# Revit family: 879-003X99-001-DN300-600
name_source: partatom
category: Pipe Accessories
units: mm (PartAtom-declared; Revit-internal decimal feet)

## family parameters
Always vertical = Yes
Cut with Voids When Loaded = No
Part Type = Valve - Breaks Into
Round Connector Dimension = Use Diameter
Shared = No
Work Plane-Based = No

## types (59) — shared parameters
879-0300-00-04400309999 = DN300_PN10
879-0300-00-04400319999 = DN300_PN10
879-0300-00-044003199A0 = DN300_PN10
879-0300-00-04400329999 = DN300_PN10
879-0300-00-04400339999 = DN300_PN10
879-0300-00-14400309999 = DN300_PN16
879-0300-00-14400319999 = DN300_PN16
879-0300-00-144003199A0 = DN300_PN16
879-0300-00-14400329999 = DN300_PN16
879-0300-00-14400339999 = DN300_PN16
879-0350-00-04400309999 = DN350_PN10
879-0350-00-04400319999 = DN350_PN10
879-0350-00-044003199A0 = DN350_PN10
879-0350-00-04400329999 = DN350_PN10
879-0350-00-04400339999 = DN350_PN10
879-0350-00-14400309999 = DN350_PN16
879-0350-00-14400319999 = DN350_PN16
879-0350-00-144003199A0 = DN350_PN16
879-0350-00-14400329999 = DN350_PN16
879-0350-00-14400339999 = DN350_PN16
879-0400-00-04400309999 = DN400_PN10
879-0400-00-04400319999 = DN400_PN10
879-0400-00-044003199A0 = DN400_PN10
879-0400-00-04400329999 = DN400_PN10
879-0400-00-04400339999 = DN400_PN10
879-0400-00-14400309999 = DN400_PN16
879-0400-00-14400319999 = DN400_PN16
879-0400-00-144003199A0 = DN400_PN16
879-0400-00-14400329999 = DN400_PN16
879-0400-00-14400339999 = DN400_PN16
879-0450-00-04400309999 = DN450_PN10
879-0450-00-04400319999 = DN450_PN10
879-0450-00-044003199A0 = DN450_PN10
879-0450-00-04400329999 = DN450_PN10
879-0450-00-04400339999 = DN450_PN10
879-0450-00-14400309999 = DN450_PN16
879-0450-00-14400319999 = DN450_PN16
879-0450-00-144003199A0 = DN450_PN16
879-0450-00-14400329999 = DN450_PN16
879-0450-00-14400339999 = DN450_PN16
879-0500-00-04400309999 = DN500_PN10
879-0500-00-04400319999 = DN500_PN10
879-0500-00-044003199A0 = DN500_PN10
879-0500-00-04400329999 = DN500_PN10
879-0500-00-04400339999 = DN500_PN10
879-0500-00-14400309999 = DN500_PN16
879-0500-00-14400319999 = DN500_PN16
879-0500-00-144003199A0 = DN500_PN16
879-0500-00-14400329999 = DN500_PN16
879-0500-00-14400339999 = DN500_PN16
879-0600-00-04400309999 = DN600_PN10
879-0600-00-04400319999 = DN600_PN10
879-0600-00-044003199A0 = DN600_PN10
879-0600-00-04400329999 = DN600_PN10
879-0600-00-04400339999 = DN600_PN10
879-0600-00-14400309999 = DN600_PN16
879-0600-00-14400319999 = DN600_PN16
879-0600-00-144003199A0 = DN600_PN16
879-0600-00-14400329999 = DN600_PN16
879-0600-00-14400339999 = DN600_PN16
Body_wall_thickness = 10 mm  [stored 0.0328084 ft]
Description_ = AVK ONE WAY ALTITUDE LEVEL CONTROL VALVE
Search_Table = 879-003X99-001-DN300-600
URL product pages = https://www.avkvalves.com

## per-type parameters (varying)
- 879-0300-00-04400309999_DN300_PN10: Body_Collar_Dia=77 mm; Body_Collar_Dia_2=53 mm; Body_Flange_Dia=243 mm; Body_Flange_Dia_2=266 mm; Body_Height_1=213 mm; Body_Height_2=106 mm; Body_Height_3=95 mm; Body_Height_4=121 mm; Body_Top_Dia=31 mm  [stored 0.101706 ft]; Body_Top_Dia_2=26 mm; Body_With_Dia=106 mm; Body_With_Dia_1=213 mm; Body_With_Dia_2=213 mm; Bolt_support=654 mm; Bolt_support_2=327 mm; Bolt_support_Dia=20 mm  [stored 0.0656168 ft]; Bolt_support_lenght=170 mm; Bolt_support_lenght_2=180 mm; Bottom_profile=75 mm; D1=185 mm; D3=223 mm; DN=300 mm; Fillet_Length=10 mm  [stored 0.0328084 ft]; Fillet_Length_Ref=30 mm  [stored 0.0984252 ft]; Flange_thickness=25 mm  [stored 0.082021 ft]; H=865 mm; H3_Ref=855 mm; ID=150 mm; L=850 mm; L_Ref=401 mm; NV_Dia=190 mm; PG_Dia=100 mm; PG_Ref=142 mm; PG_depth=14 mm  [stored 0.0459318 ft]; PG_height=519 mm; PG_height_1=469 mm; PG_ref=160 mm; PR_1=63 mm; P_lenght=116 mm; Pilot_Dia_1=53 mm; Pilot_Dia_2=105 mm; Pilot_Dia_3=35 mm  [stored 0.114829 ft]; Pilot_Dia_4=18 mm; Pilot_Dia_5=12 mm  [stored 0.0393701 ft]; Pilot_top_1=530 mm; Pilot_top_ref=92 mm; Profile1_Height=326 mm; Profile1_Length=60 mm; Profile1_Length_2=40 mm  [stored 0.131234 ft]; Profile_Dia=10 mm  [stored 0.0328084 ft]; Profile_Dia_2=10 mm  [stored 0.0328084 ft]; Profile_Dia_3=20 mm  [stored 0.0656168 ft]; Profile_Dia_Ref=5 mm  [stored 0.0164042 ft]; Profile_Dia_Ref_2=20 mm  [stored 0.0656168 ft]; Profile_height ref=30 mm  [stored 0.0984252 ft]; T_Height=277 mm; T_Height_2=237 mm; T_Height_Ref_1=40 mm  [stored 0.131234 ft]; T_Height_Ref_2=46 mm  [stored 0.150919 ft]; T_ref=481 mm; Top_Profile=392 mm; Top_Profile_Ref=397 mm; W=835 mm; W_Ref=821 mm
- 879-0300-00-04400319999_DN300_PN10: Body_Collar_Dia=77 mm; Body_Collar_Dia_2=53 mm; Body_Flange_Dia=243 mm; Body_Flange_Dia_2=266 mm; Body_Height_1=213 mm; Body_Height_2=106 mm; Body_Height_3=106 mm; Body_Height_4=121 mm; Body_Top_Dia=31 mm  [stored 0.101706 ft]; Body_Top_Dia_2=26 mm; Body_With_Dia=106 mm; Body_With_Dia_1=213 mm; Body_With_Dia_2=213 mm; Bolt_support=654 mm; Bolt_support_2=327 mm; Bolt_support_Dia=20 mm  [stored 0.0656168 ft]; Bolt_support_lenght=170 mm; Bolt_support_lenght_2=180 mm; Bottom_profile=75 mm; D1=185 mm; D3=223 mm; DN=300 mm; Fillet_Length=10 mm  [stored 0.0328084 ft]; Fillet_Length_Ref=30 mm  [stored 0.0984252 ft]; Flange_thickness=25 mm  [stored 0.082021 ft]; H=865 mm; H3_Ref=855 mm; ID=150 mm; L=850 mm; L_Ref=401 mm; NV_Dia=190 mm; PG_Dia=100 mm; PG_Ref=142 mm; PG_depth=14 mm  [stored 0.0459318 ft]; PG_height=549 mm; PG_height_1=499 mm; PG_ref=160 mm; PR_1=54 mm; P_lenght=116 mm; Pilot_Dia_1=53 mm; Pilot_Dia_2=105 mm; Pilot_Dia_3=35 mm  [stored 0.114829 ft]; Pilot_Dia_4=18 mm; Pilot_Dia_5=12 mm  [stored 0.0393701 ft]; Pilot_top_1=536 mm; Pilot_top_ref=86 mm; Profile1_Height=365 mm; Profile1_Length=60 mm; Profile1_Length_2=40 mm  [stored 0.131234 ft]; Profile_Dia=10 mm  [stored 0.0328084 ft]; Profile_Dia_2=10 mm  [stored 0.0328084 ft]; Profile_Dia_3=20 mm  [stored 0.0656168 ft]; Profile_Dia_Ref=5 mm  [stored 0.0164042 ft]; Profile_Dia_Ref_2=20 mm  [stored 0.0656168 ft]; Profile_height ref=30 mm  [stored 0.0984252 ft]; T_Height=238 mm; T_Height_2=204 mm; T_Height_Ref_1=34 mm; T_Height_Ref_2=40 mm  [stored 0.131234 ft]; T_ref=502 mm; Top_Profile=392 mm; Top_Profile_Ref=397 mm; W=835 mm; W_Ref=821 mm
- 879-0300-00-044003199A0_DN300_PN10: Body_Collar_Dia=77 mm; Body_Collar_Dia_2=53 mm; Body_Flange_Dia=243 mm; Body_Flange_Dia_2=266 mm; Body_Height_1=213 mm; Body_Height_2=106 mm; Body_Height_3=95 mm; Body_Height_4=121 mm; Body_Top_Dia=31 mm  [stored 0.101706 ft]; Body_Top_Dia_2=26 mm; Body_With_Dia=106 mm; Body_With_Dia_1=213 mm; Body_With_Dia_2=213 mm; Bolt_support=654 mm; Bolt_support_2=327 mm; Bolt_support_Dia=20 mm  [stored 0.0656168 ft]; Bolt_support_lenght=170 mm; Bolt_support_lenght_2=180 mm; Bottom_profile=75 mm; D1=185 mm; D3=223 mm; DN=300 mm; Fillet_Length=10 mm  [stored 0.0328084 ft]; Fillet_Length_Ref=30 mm  [stored 0.0984252 ft]; Flange_thickness=25 mm  [stored 0.082021 ft]; H=881 mm; H3_Ref=871 mm; ID=150 mm; L=850 mm; L_Ref=401 mm; NV_Dia=190 mm; PG_Dia=100 mm; PG_Ref=142 mm; PG_depth=14 mm  [stored 0.0459318 ft]; PG_height=537 mm; PG_height_1=487 mm; PG_ref=160 mm; PR_1=62 mm; P_lenght=120 mm; Pilot_Dia_1=55 mm; Pilot_Dia_2=109 mm; Pilot_Dia_3=36 mm  [stored 0.11811 ft]; Pilot_Dia_4=18 mm; Pilot_Dia_5=12 mm  [stored 0.0393701 ft]; Pilot_top_1=538 mm; Pilot_top_ref=100 mm; Profile1_Height=345 mm; Profile1_Length=60 mm; Profile1_Length_2=40 mm  [stored 0.131234 ft]; Profile_Dia=10 mm  [stored 0.0328084 ft]; Profile_Dia_2=10 mm  [stored 0.0328084 ft]; Profile_Dia_3=20 mm  [stored 0.0656168 ft]; Profile_Dia_Ref=5 mm  [stored 0.0164042 ft]; Profile_Dia_Ref_2=20 mm  [stored 0.0656168 ft]; Profile_height ref=30 mm  [stored 0.0984252 ft]; T_Height=274 mm; T_Height_2=234 mm; T_Height_Ref_1=39 mm  [stored 0.127953 ft]; T_Height_Ref_2=46 mm  [stored 0.150919 ft]; T_ref=499 mm; Top_Profile=392 mm; Top_Profile_Ref=397 mm; W=835 mm; W_Ref=821 mm
- 879-0300-00-04400329999_DN300_PN10: Body_Collar_Dia=77 mm; Body_Collar_Dia_2=53 mm; Body_Flange_Dia=243 mm; Body_Flange_Dia_2=266 mm; Body_Height_1=213 mm; Body_Height_2=106 mm; Body_Height_3=95 mm; Body_Height_4=121 mm; Body_Top_Dia=31 mm  [stored 0.101706 ft]; Body_Top_Dia_2=26 mm; Body_With_Dia=106 mm; Body_With_Dia_1=213 mm; Body_With_Dia_2=213 mm; Bolt_support=654 mm; Bolt_support_2=327 mm; Bolt_support_Dia=20 mm  [stored 0.0656168 ft]; Bolt_support_lenght=170 mm; Bolt_support_lenght_2=180 mm; Bottom_profile=75 mm; D1=185 mm; D3=223 mm; DN=300 mm; Fillet_Length=10 mm  [stored 0.0328084 ft]; Fillet_Length_Ref=30 mm  [stored 0.0984252 ft]; Flange_thickness=25 mm  [stored 0.082021 ft]; H=865 mm; H3_Ref=855 mm; ID=150 mm; L=850 mm; L_Ref=401 mm; NV_Dia=190 mm; PG_Dia=100 mm; PG_Ref=142 mm; PG_depth=14 mm  [stored 0.0459318 ft]; PG_height=533 mm; PG_height_1=483 mm; PG_ref=160 mm; PR_1=58 mm; P_lenght=120 mm; Pilot_Dia_1=55 mm; Pilot_Dia_2=109 mm; Pilot_Dia_3=36 mm  [stored 0.11811 ft]; Pilot_Dia_4=18 mm; Pilot_Dia_5=12 mm  [stored 0.0393701 ft]; Pilot_top_1=530 mm; Pilot_top_ref=92 mm; Profile1_Height=345 mm; Profile1_Length=60 mm; Profile1_Length_2=40 mm  [stored 0.131234 ft]; Profile_Dia=10 mm  [stored 0.0328084 ft]; Profile_Dia_2=10 mm  [stored 0.0328084 ft]; Profile_Dia_3=20 mm  [stored 0.0656168 ft]; Profile_Dia_Ref=5 mm  [stored 0.0164042 ft]; Profile_Dia_Ref_2=20 mm  [stored 0.0656168 ft]; Profile_height ref=30 mm  [stored 0.0984252 ft]; T_Height=258 mm; T_Height_2=221 mm; T_Height_Ref_1=37 mm; T_Height_Ref_2=43 mm; T_ref=491 mm; Top_Profile=392 mm; Top_Profile_Ref=397 mm; W=835 mm; W_Ref=821 mm
- 879-0300-00-04400339999_DN300_PN10: Body_Collar_Dia=77 mm; Body_Collar_Dia_2=53 mm; Body_Flange_Dia=243 mm; Body_Flange_Dia_2=266 mm; Body_Height_1=213 mm; Body_Height_2=106 mm; Body_Height_3=95 mm; Body_Height_4=121 mm; Body_Top_Dia=31 mm  [stored 0.101706 ft]; Body_Top_Dia_2=26 mm; Body_With_Dia=106 mm; Body_With_Dia_1=213 mm; Body_With_Dia_2=213 mm; Bolt_support=654 mm; Bolt_support_2=327 mm; Bolt_support_Dia=20 mm  [stored 0.0656168 ft]; Bolt_support_lenght=170 mm; Bolt_support_lenght_2=180 mm; Bottom_profile=75 mm; D1=185 mm; D3=223 mm; DN=300 mm; Fillet_Length=10 mm  [stored 0.0328084 ft]; Fillet_Length_Ref=30 mm  [stored 0.0984252 ft]; Flange_thickness=25 mm  [stored 0.082021 ft]; H=865 mm; H3_Ref=855 mm; ID=150 mm; L=850 mm; L_Ref=401 mm; NV_Dia=190 mm; PG_Dia=100 mm; PG_Ref=142 mm; PG_depth=14 mm  [stored 0.0459318 ft]; PG_height=519 mm; PG_height_1=469 mm; PG_ref=160 mm; PR_1=63 mm; P_lenght=116 mm; Pilot_Dia_1=53 mm; Pilot_Dia_2=105 mm; Pilot_Dia_3=35 mm  [stored 0.114829 ft]; Pilot_Dia_4=18 mm; Pilot_Dia_5=12 mm  [stored 0.0393701 ft]; Pilot_top_1=530 mm; Pilot_top_ref=92 mm; Profile1_Height=326 mm; Profile1_Length=60 mm; Profile1_Length_2=40 mm  [stored 0.131234 ft]; Profile_Dia=10 mm  [stored 0.0328084 ft]; Profile_Dia_2=10 mm  [stored 0.0328084 ft]; Profile_Dia_3=20 mm  [stored 0.0656168 ft]; Profile_Dia_Ref=5 mm  [stored 0.0164042 ft]; Profile_Dia_Ref_2=20 mm  [stored 0.0656168 ft]; Profile_height ref=30 mm  [stored 0.0984252 ft]; T_Height=277 mm; T_Height_2=237 mm; T_Height_Ref_1=40 mm  [stored 0.131234 ft]; T_Height_Ref_2=46 mm  [stored 0.150919 ft]; T_ref=481 mm; Top_Profile=392 mm; Top_Profile_Ref=397 mm; W=835 mm; W_Ref=821 mm
- 879-0300-00-14400309999_DN300_PN16: Body_Collar_Dia=77 mm; Body_Collar_Dia_2=53 mm; Body_Flange_Dia=243 mm; Body_Flange_Dia_2=266 mm; Body_Height_1=213 mm; Body_Height_2=106 mm; Body_Height_3=106 mm; Body_Height_4=121 mm; Body_Top_Dia=31 mm  [stored 0.101706 ft]; Body_Top_Dia_2=26 mm; Body_With_Dia=106 mm; Body_With_Dia_1=213 mm; Body_With_Dia_2=213 mm; Bolt_support=654 mm; Bolt_support_2=327 mm; Bolt_support_Dia=20 mm  [stored 0.0656168 ft]; Bolt_support_lenght=170 mm; Bolt_support_lenght_2=180 mm; Bottom_profile=75 mm; D1=185 mm; D3=230 mm; DN=301 mm; Fillet_Length=10 mm  [stored 0.0328084 ft]; Fillet_Length_Ref=30 mm  [stored 0.0984252 ft]; Flange_thickness=25 mm  [stored 0.082021 ft]; H=865 mm; H3_Ref=855 mm; ID=150 mm; L=850 mm; L_Ref=401 mm; NV_Dia=190 mm; PG_Dia=100 mm; PG_Ref=142 mm; PG_depth=14 mm  [stored 0.0459318 ft]; PG_height=547 mm; PG_height_1=497 mm; PG_ref=160 mm; PR_1=52 mm; P_lenght=116 mm; Pilot_Dia_1=53 mm; Pilot_Dia_2=105 mm; Pilot_Dia_3=35 mm  [stored 0.114829 ft]; Pilot_Dia_4=18 mm; Pilot_Dia_5=12 mm  [stored 0.0393701 ft]; Pilot_top_1=532 mm; Pilot_top_ref=83 mm; Profile1_Height=365 mm; Profile1_Length=62 mm; Profile1_Length_2=41 mm; Profile_Dia=10 mm  [stored 0.0328084 ft]; Profile_Dia_2=10 mm  [stored 0.0328084 ft]; Profile_Dia_3=20 mm  [stored 0.0656168 ft]; Profile_Dia_Ref=5 mm  [stored 0.0164042 ft]; Profile_Dia_Ref_2=20 mm  [stored 0.0656168 ft]; Profile_height ref=30 mm  [stored 0.0984252 ft]; T_Height=230 mm; T_Height_2=197 mm; T_Height_Ref_1=33 mm; T_Height_Ref_2=38 mm  [stored 0.124672 ft]; T_ref=499 mm; Top_Profile=392 mm; Top_Profile_Ref=397 mm; W=835 mm; W_Ref=821 mm
- 879-0300-00-14400319999_DN300_PN16: Body_Collar_Dia=77 mm; Body_Collar_Dia_2=53 mm; Body_Flange_Dia=243 mm; Body_Flange_Dia_2=266 mm; Body_Height_1=213 mm; Body_Height_2=106 mm; Body_Height_3=95 mm; Body_Height_4=121 mm; Body_Top_Dia=31 mm  [stored 0.101706 ft]; Body_Top_Dia_2=26 mm; Body_With_Dia=106 mm; Body_With_Dia_1=213 mm; Body_With_Dia_2=213 mm; Bolt_support=654 mm; Bolt_support_2=327 mm; Bolt_support_Dia=20 mm  [stored 0.0656168 ft]; Bolt_support_lenght=170 mm; Bolt_support_lenght_2=180 mm; Bottom_profile=75 mm; D1=185 mm; D3=230 mm; DN=301 mm; Fillet_Length=10 mm  [stored 0.0328084 ft]; Fillet_Length_Ref=30 mm  [stored 0.0984252 ft]; Flange_thickness=25 mm  [stored 0.082021 ft]; H=865 mm; H3_Ref=855 mm; ID=150 mm; L=850 mm; L_Ref=401 mm; NV_Dia=190 mm; PG_Dia=100 mm; PG_Ref=142 mm; PG_depth=14 mm  [stored 0.0459318 ft]; PG_height=532 mm; PG_height_1=482 mm; PG_ref=160 mm; PR_1=57 mm; P_lenght=120 mm; Pilot_Dia_1=55 mm; Pilot_Dia_2=109 mm; Pilot_Dia_3=36 mm  [stored 0.11811 ft]; Pilot_Dia_4=18 mm; Pilot_Dia_5=12 mm  [stored 0.0393701 ft]; Pilot_top_1=527 mm; Pilot_top_ref=88 mm; Profile1_Height=345 mm; Profile1_Length=62 mm; Profile1_Length_2=41 mm; Profile_Dia=10 mm  [stored 0.0328084 ft]; Profile_Dia_2=10 mm  [stored 0.0328084 ft]; Profile_Dia_3=20 mm  [stored 0.0656168 ft]; Profile_Dia_Ref=5 mm  [stored 0.0164042 ft]; Profile_Dia_Ref_2=20 mm  [stored 0.0656168 ft]; Profile_height ref=30 mm  [stored 0.0984252 ft]; T_Height=250 mm; T_Height_2=214 mm; T_Height_Ref_1=36 mm  [stored 0.11811 ft]; T_Height_Ref_2=42 mm  [stored 0.137795 ft]; T_ref=488 mm; Top_Profile=392 mm; Top_Profile_Ref=397 mm; W=835 mm; W_Ref=821 mm
- 879-0300-00-144003199A0_DN300_PN16: Body_Collar_Dia=77 mm; Body_Collar_Dia_2=53 mm; Body_Flange_Dia=243 mm; Body_Flange_Dia_2=266 mm; Body_Height_1=213 mm; Body_Height_2=106 mm; Body_Height_3=95 mm; Body_Height_4=121 mm; Body_Top_Dia=31 mm  [stored 0.101706 ft]; Body_Top_Dia_2=26 mm; Body_With_Dia=106 mm; Body_With_Dia_1=213 mm; Body_With_Dia_2=213 mm; Bolt_support=654 mm; Bolt_support_2=327 mm; Bolt_support_Dia=20 mm  [stored 0.0656168 ft]; Bolt_support_lenght=170 mm; Bolt_support_lenght_2=180 mm; Bottom_profile=75 mm; D1=185 mm; D3=230 mm; DN=301 mm; Fillet_Length=10 mm  [stored 0.0328084 ft]; Fillet_Length_Ref=30 mm  [stored 0.0984252 ft]; Flange_thickness=25 mm  [stored 0.082021 ft]; H=881 mm; H3_Ref=871 mm; ID=150 mm; L=850 mm; L_Ref=401 mm; NV_Dia=190 mm; PG_Dia=100 mm; PG_Ref=142 mm; PG_depth=14 mm  [stored 0.0459318 ft]; PG_height=535 mm; PG_height_1=485 mm; PG_ref=160 mm; PR_1=60 mm; P_lenght=120 mm; Pilot_Dia_1=55 mm; Pilot_Dia_2=109 mm; Pilot_Dia_3=36 mm  [stored 0.11811 ft]; Pilot_Dia_4=18 mm; Pilot_Dia_5=12 mm  [stored 0.0393701 ft]; Pilot_top_1=535 mm; Pilot_top_ref=96 mm; Profile1_Height=345 mm; Profile1_Length=62 mm; Profile1_Length_2=41 mm; Profile_Dia=10 mm  [stored 0.0328084 ft]; Profile_Dia_2=10 mm  [stored 0.0328084 ft]; Profile_Dia_3=20 mm  [stored 0.0656168 ft]; Profile_Dia_Ref=5 mm  [stored 0.0164042 ft]; Profile_Dia_Ref_2=20 mm  [stored 0.0656168 ft]; Profile_height ref=30 mm  [stored 0.0984252 ft]; T_Height=266 mm; T_Height_2=228 mm; T_Height_Ref_1=38 mm  [stored 0.124672 ft]; T_Height_Ref_2=44 mm; T_ref=495 mm; Top_Profile=392 mm; Top_Profile_Ref=397 mm; W=835 mm; W_Ref=821 mm
- 879-0300-00-14400329999_DN300_PN16: Body_Collar_Dia=77 mm; Body_Collar_Dia_2=53 mm; Body_Flange_Dia=243 mm; Body_Flange_Dia_2=266 mm; Body_Height_1=213 mm; Body_Height_2=106 mm; Body_Height_3=95 mm; Body_Height_4=121 mm; Body_Top_Dia=31 mm  [stored 0.101706 ft]; Body_Top_Dia_2=26 mm; Body_With_Dia=106 mm; Body_With_Dia_1=213 mm; Body_With_Dia_2=213 mm; Bolt_support=654 mm; Bolt_support_2=327 mm; Bolt_support_Dia=20 mm  [stored 0.0656168 ft]; Bolt_support_lenght=170 mm; Bolt_support_lenght_2=180 mm; Bottom_profile=75 mm; D1=185 mm; D3=230 mm; DN=301 mm; Fillet_Length=10 mm  [stored 0.0328084 ft]; Fillet_Length_Ref=30 mm  [stored 0.0984252 ft]; Flange_thickness=25 mm  [stored 0.082021 ft]; H=865 mm; H3_Ref=855 mm; ID=150 mm; L=850 mm; L_Ref=401 mm; NV_Dia=190 mm; PG_Dia=100 mm; PG_Ref=142 mm; PG_depth=14 mm  [stored 0.0459318 ft]; PG_height=517 mm; PG_height_1=467 mm; PG_ref=160 mm; PR_1=61 mm; P_lenght=116 mm; Pilot_Dia_1=53 mm; Pilot_Dia_2=105 mm; Pilot_Dia_3=35 mm  [stored 0.114829 ft]; Pilot_Dia_4=18 mm; Pilot_Dia_5=12 mm  [stored 0.0393701 ft]; Pilot_top_1=527 mm; Pilot_top_ref=88 mm; Profile1_Height=326 mm; Profile1_Length=62 mm; Profile1_Length_2=41 mm; Profile_Dia=10 mm  [stored 0.0328084 ft]; Profile_Dia_2=10 mm  [stored 0.0328084 ft]; Profile_Dia_3=20 mm  [stored 0.0656168 ft]; Profile_Dia_Ref=5 mm  [stored 0.0164042 ft]; Profile_Dia_Ref_2=20 mm  [stored 0.0656168 ft]; Profile_height ref=30 mm  [stored 0.0984252 ft]; T_Height=269 mm; T_Height_2=231 mm; T_Height_Ref_1=38 mm  [stored 0.124672 ft]; T_Height_Ref_2=45 mm  [stored 0.147638 ft]; T_ref=478 mm; Top_Profile=392 mm; Top_Profile_Ref=397 mm; W=835 mm; W_Ref=821 mm
- 879-0300-00-14400339999_DN300_PN16: Body_Collar_Dia=77 mm; Body_Collar_Dia_2=53 mm; Body_Flange_Dia=243 mm; Body_Flange_Dia_2=266 mm; Body_Height_1=213 mm; Body_Height_2=106 mm; Body_Height_3=106 mm; Body_Height_4=121 mm; Body_Top_Dia=31 mm  [stored 0.101706 ft]; Body_Top_Dia_2=26 mm; Body_With_Dia=106 mm; Body_With_Dia_1=213 mm; Body_With_Dia_2=213 mm; Bolt_support=654 mm; Bolt_support_2=327 mm; Bolt_support_Dia=20 mm  [stored 0.0656168 ft]; Bolt_support_lenght=170 mm; Bolt_support_lenght_2=180 mm; Bottom_profile=75 mm; D1=185 mm; D3=230 mm; DN=301 mm; Fillet_Length=10 mm  [stored 0.0328084 ft]; Fillet_Length_Ref=30 mm  [stored 0.0984252 ft]; Flange_thickness=25 mm  [stored 0.082021 ft]; H=865 mm; H3_Ref=855 mm; ID=150 mm; L=850 mm; L_Ref=401 mm; NV_Dia=190 mm; PG_Dia=100 mm; PG_Ref=142 mm; PG_depth=14 mm  [stored 0.0459318 ft]; PG_height=547 mm; PG_height_1=497 mm; PG_ref=160 mm; PR_1=52 mm; P_lenght=116 mm; Pilot_Dia_1=53 mm; Pilot_Dia_2=105 mm; Pilot_Dia_3=35 mm  [stored 0.114829 ft]; Pilot_Dia_4=18 mm; Pilot_Dia_5=12 mm  [stored 0.0393701 ft]; Pilot_top_1=532 mm; Pilot_top_ref=83 mm; Profile1_Height=365 mm; Profile1_Length=62 mm; Profile1_Length_2=41 mm; Profile_Dia=10 mm  [stored 0.0328084 ft]; Profile_Dia_2=10 mm  [stored 0.0328084 ft]; Profile_Dia_3=20 mm  [stored 0.0656168 ft]; Profile_Dia_Ref=5 mm  [stored 0.0164042 ft]; Profile_Dia_Ref_2=20 mm  [stored 0.0656168 ft]; Profile_height ref=30 mm  [stored 0.0984252 ft]; T_Height=230 mm; T_Height_2=197 mm; T_Height_Ref_1=33 mm; T_Height_Ref_2=38 mm  [stored 0.124672 ft]; T_ref=499 mm; Top_Profile=392 mm; Top_Profile_Ref=397 mm; W=835 mm; W_Ref=821 mm
- 879-0350-00-04400309999_DN350_PN10: Body_Collar_Dia=89 mm; Body_Collar_Dia_2=61 mm; Body_Flange_Dia=280 mm; Body_Flange_Dia_2=306 mm; Body_Height_1=245 mm; Body_Height_2=123 mm; Body_Height_3=98 mm; Body_Height_4=138 mm; Body_Top_Dia=36 mm  [stored 0.11811 ft]; Body_Top_Dia_2=30 mm  [stored 0.0984252 ft]; Body_With_Dia=123 mm; Body_With_Dia_1=245 mm; Body_With_Dia_2=245 mm; Bolt_support=754 mm; Bolt_support_2=377 mm; Bolt_support_Dia=30 mm  [stored 0.0984252 ft]; Bolt_support_lenght=195 mm; Bolt_support_lenght_2=205 mm; Bottom_profile=88 mm; D1=215 mm; D3=253 mm; DN=350 mm; Fillet_Length=15 mm  [stored 0.0492126 ft]; Fillet_Length_Ref=45 mm  [stored 0.147638 ft]; Flange_thickness=27 mm  [stored 0.0885827 ft]; H=945 mm; H3_Ref=930 mm; ID=175 mm; L=980 mm; L_Ref=464 mm; NV_Dia=200 mm; PG_Dia=117 mm; PG_Ref=163 mm; PG_depth=21 mm  [stored 0.0688976 ft]; PG_height=607 mm; PG_height_1=548 mm; PG_ref=185 mm; PR_1=55 mm; P_lenght=133 mm; Pilot_Dia_1=61 mm; Pilot_Dia_2=121 mm; Pilot_Dia_3=40 mm  [stored 0.131234 ft]; Pilot_Dia_4=20 mm  [stored 0.0656168 ft]; Pilot_Dia_5=13 mm; Pilot_top_1=579 mm; Pilot_top_ref=89 mm; Profile1_Height=395 mm; Profile1_Length=68 mm; Profile1_Length_2=45 mm  [stored 0.147638 ft]; Profile_Dia=15 mm  [stored 0.0492126 ft]; Profile_Dia_2=15 mm  [stored 0.0492126 ft]; Profile_Dia_3=30 mm  [stored 0.0984252 ft]; Profile_Dia_Ref=8 mm  [stored 0.0262467 ft]; Profile_Dia_Ref_2=30 mm  [stored 0.0984252 ft]; Profile_height ref=40 mm  [stored 0.131234 ft]; T_Height=243 mm; T_Height_2=208 mm; T_Height_Ref_1=35 mm  [stored 0.114829 ft]; T_Height_Ref_2=40 mm  [stored 0.131234 ft]; T_ref=545 mm; Top_Profile=452 mm; Top_Profile_Ref=457 mm; W=890 mm; W_Ref=869 mm
- 879-0350-00-04400319999_DN350_PN10: Body_Collar_Dia=89 mm; Body_Collar_Dia_2=61 mm; Body_Flange_Dia=280 mm; Body_Flange_Dia_2=306 mm; Body_Height_1=245 mm; Body_Height_2=123 mm; Body_Height_3=98 mm; Body_Height_4=138 mm; Body_Top_Dia=36 mm  [stored 0.11811 ft]; Body_Top_Dia_2=30 mm  [stored 0.0984252 ft]; Body_With_Dia=123 mm; Body_With_Dia_1=245 mm; Body_With_Dia_2=245 mm; Bolt_support=754 mm; Bolt_support_2=377 mm; Bolt_support_Dia=30 mm  [stored 0.0984252 ft]; Bolt_support_lenght=195 mm; Bolt_support_lenght_2=205 mm; Bottom_profile=88 mm; D1=215 mm; D3=253 mm; DN=350 mm; Fillet_Length=15 mm  [stored 0.0492126 ft]; Fillet_Length_Ref=45 mm  [stored 0.147638 ft]; Flange_thickness=27 mm  [stored 0.0885827 ft]; H=945 mm; H3_Ref=930 mm; ID=175 mm; L=980 mm; L_Ref=464 mm; NV_Dia=200 mm; PG_Dia=117 mm; PG_Ref=163 mm; PG_depth=21 mm  [stored 0.0688976 ft]; PG_height=607 mm; PG_height_1=548 mm; PG_ref=185 mm; PR_1=55 mm; P_lenght=133 mm; Pilot_Dia_1=61 mm; Pilot_Dia_2=121 mm; Pilot_Dia_3=40 mm  [stored 0.131234 ft]; Pilot_Dia_4=20 mm  [stored 0.0656168 ft]; Pilot_Dia_5=13 mm; Pilot_top_1=579 mm; Pilot_top_ref=89 mm; Profile1_Height=395 mm; Profile1_Length=68 mm; Profile1_Length_2=45 mm  [stored 0.147638 ft]; Profile_Dia=15 mm  [stored 0.0492126 ft]; Profile_Dia_2=15 mm  [stored 0.0492126 ft]; Profile_Dia_3=30 mm  [stored 0.0984252 ft]; Profile_Dia_Ref=8 mm  [stored 0.0262467 ft]; Profile_Dia_Ref_2=30 mm  [stored 0.0984252 ft]; Profile_height ref=40 mm  [stored 0.131234 ft]; T_Height=243 mm; T_Height_2=208 mm; T_Height_Ref_1=35 mm  [stored 0.114829 ft]; T_Height_Ref_2=40 mm  [stored 0.131234 ft]; T_ref=545 mm; Top_Profile=452 mm; Top_Profile_Ref=457 mm; W=890 mm; W_Ref=869 mm
- 879-0350-00-044003199A0_DN350_PN10: Body_Collar_Dia=89 mm; Body_Collar_Dia_2=61 mm; Body_Flange_Dia=280 mm; Body_Flange_Dia_2=306 mm; Body_Height_1=245 mm; Body_Height_2=123 mm; Body_Height_3=89 mm; Body_Height_4=138 mm; Body_Top_Dia=36 mm  [stored 0.11811 ft]; Body_Top_Dia_2=30 mm  [stored 0.0984252 ft]; Body_With_Dia=123 mm; Body_With_Dia_1=245 mm; Body_With_Dia_2=245 mm; Bolt_support=754 mm; Bolt_support_2=377 mm; Bolt_support_Dia=30 mm  [stored 0.0984252 ft]; Bolt_support_lenght=195 mm; Bolt_support_lenght_2=205 mm; Bottom_profile=88 mm; D1=215 mm; D3=253 mm; DN=350 mm; Fillet_Length=15 mm  [stored 0.0492126 ft]; Fillet_Length_Ref=45 mm  [stored 0.147638 ft]; Flange_thickness=27 mm  [stored 0.0885827 ft]; H=959 mm; H3_Ref=944 mm; ID=175 mm; L=980 mm; L_Ref=464 mm; NV_Dia=200 mm; PG_Dia=117 mm; PG_Ref=163 mm; PG_depth=21 mm  [stored 0.0688976 ft]; PG_height=610 mm; PG_height_1=551 mm; PG_ref=185 mm; PR_1=58 mm; P_lenght=139 mm; Pilot_Dia_1=63 mm; Pilot_Dia_2=126 mm; Pilot_Dia_3=42 mm  [stored 0.137795 ft]; Pilot_Dia_4=21 mm  [stored 0.0688976 ft]; Pilot_Dia_5=14 mm  [stored 0.0459318 ft]; Pilot_top_1=582 mm; Pilot_top_ref=100 mm; Profile1_Height=395 mm; Profile1_Length=68 mm; Profile1_Length_2=45 mm  [stored 0.147638 ft]; Profile_Dia=15 mm  [stored 0.0492126 ft]; Profile_Dia_2=15 mm  [stored 0.0492126 ft]; Profile_Dia_3=30 mm  [stored 0.0984252 ft]; Profile_Dia_Ref=8 mm  [stored 0.0262467 ft]; Profile_Dia_Ref_2=30 mm  [stored 0.0984252 ft]; Profile_height ref=40 mm  [stored 0.131234 ft]; T_Height=257 mm; T_Height_2=220 mm; T_Height_Ref_1=37 mm; T_Height_Ref_2=43 mm; T_ref=551 mm; Top_Profile=452 mm; Top_Profile_Ref=457 mm; W=890 mm; W_Ref=869 mm
- 879-0350-00-04400329999_DN350_PN10: Body_Collar_Dia=89 mm; Body_Collar_Dia_2=61 mm; Body_Flange_Dia=280 mm; Body_Flange_Dia_2=306 mm; Body_Height_1=245 mm; Body_Height_2=123 mm; Body_Height_3=89 mm; Body_Height_4=138 mm; Body_Top_Dia=36 mm  [stored 0.11811 ft]; Body_Top_Dia_2=30 mm  [stored 0.0984252 ft]; Body_With_Dia=123 mm; Body_With_Dia_1=245 mm; Body_With_Dia_2=245 mm; Bolt_support=754 mm; Bolt_support_2=377 mm; Bolt_support_Dia=30 mm  [stored 0.0984252 ft]; Bolt_support_lenght=195 mm; Bolt_support_lenght_2=205 mm; Bottom_profile=88 mm; D1=215 mm; D3=253 mm; DN=350 mm; Fillet_Length=15 mm  [stored 0.0492126 ft]; Fillet_Length_Ref=45 mm  [stored 0.147638 ft]; Flange_thickness=27 mm  [stored 0.0885827 ft]; H=945 mm; H3_Ref=930 mm; ID=175 mm; L=980 mm; L_Ref=464 mm; NV_Dia=200 mm; PG_Dia=117 mm; PG_Ref=163 mm; PG_depth=21 mm  [stored 0.0688976 ft]; PG_height=607 mm; PG_height_1=548 mm; PG_ref=185 mm; PR_1=55 mm; P_lenght=139 mm; Pilot_Dia_1=63 mm; Pilot_Dia_2=126 mm; Pilot_Dia_3=42 mm  [stored 0.137795 ft]; Pilot_Dia_4=21 mm  [stored 0.0688976 ft]; Pilot_Dia_5=14 mm  [stored 0.0459318 ft]; Pilot_top_1=575 mm; Pilot_top_ref=93 mm; Profile1_Height=395 mm; Profile1_Length=68 mm; Profile1_Length_2=45 mm  [stored 0.147638 ft]; Profile_Dia=15 mm  [stored 0.0492126 ft]; Profile_Dia_2=15 mm  [stored 0.0492126 ft]; Profile_Dia_3=30 mm  [stored 0.0984252 ft]; Profile_Dia_Ref=8 mm  [stored 0.0262467 ft]; Profile_Dia_Ref_2=30 mm  [stored 0.0984252 ft]; Profile_height ref=40 mm  [stored 0.131234 ft]; T_Height=243 mm; T_Height_2=208 mm; T_Height_Ref_1=35 mm  [stored 0.114829 ft]; T_Height_Ref_2=40 mm  [stored 0.131234 ft]; T_ref=545 mm; Top_Profile=452 mm; Top_Profile_Ref=457 mm; W=890 mm; W_Ref=869 mm
- 879-0350-00-04400339999_DN350_PN10: Body_Collar_Dia=89 mm; Body_Collar_Dia_2=61 mm; Body_Flange_Dia=280 mm; Body_Flange_Dia_2=306 mm; Body_Height_1=245 mm; Body_Height_2=123 mm; Body_Height_3=98 mm; Body_Height_4=138 mm; Body_Top_Dia=36 mm  [stored 0.11811 ft]; Body_Top_Dia_2=30 mm  [stored 0.0984252 ft]; Body_With_Dia=123 mm; Body_With_Dia_1=245 mm; Body_With_Dia_2=245 mm; Bolt_support=754 mm; Bolt_support_2=377 mm; Bolt_support_Dia=30 mm  [stored 0.0984252 ft]; Bolt_support_lenght=195 mm; Bolt_support_lenght_2=205 mm; Bottom_profile=88 mm; D1=215 mm; D3=253 mm; DN=350 mm; Fillet_Length=15 mm  [stored 0.0492126 ft]; Fillet_Length_Ref=45 mm  [stored 0.147638 ft]; Flange_thickness=27 mm  [stored 0.0885827 ft]; H=945 mm; H3_Ref=930 mm; ID=175 mm; L=980 mm; L_Ref=464 mm; NV_Dia=200 mm; PG_Dia=117 mm; PG_Ref=163 mm; PG_depth=21 mm  [stored 0.0688976 ft]; PG_height=607 mm; PG_height_1=548 mm; PG_ref=185 mm; PR_1=55 mm; P_lenght=133 mm; Pilot_Dia_1=61 mm; Pilot_Dia_2=121 mm; Pilot_Dia_3=40 mm  [stored 0.131234 ft]; Pilot_Dia_4=20 mm  [stored 0.0656168 ft]; Pilot_Dia_5=13 mm; Pilot_top_1=579 mm; Pilot_top_ref=89 mm; Profile1_Height=395 mm; Profile1_Length=68 mm; Profile1_Length_2=45 mm  [stored 0.147638 ft]; Profile_Dia=15 mm  [stored 0.0492126 ft]; Profile_Dia_2=15 mm  [stored 0.0492126 ft]; Profile_Dia_3=30 mm  [stored 0.0984252 ft]; Profile_Dia_Ref=8 mm  [stored 0.0262467 ft]; Profile_Dia_Ref_2=30 mm  [stored 0.0984252 ft]; Profile_height ref=40 mm  [stored 0.131234 ft]; T_Height=243 mm; T_Height_2=208 mm; T_Height_Ref_1=35 mm  [stored 0.114829 ft]; T_Height_Ref_2=40 mm  [stored 0.131234 ft]; T_ref=545 mm; Top_Profile=452 mm; Top_Profile_Ref=457 mm; W=890 mm; W_Ref=869 mm
- 879-0350-00-14400309999_DN350_PN16: Body_Collar_Dia=89 mm; Body_Collar_Dia_2=61 mm; Body_Flange_Dia=280 mm; Body_Flange_Dia_2=306 mm; Body_Height_1=245 mm; Body_Height_2=123 mm; Body_Height_3=98 mm; Body_Height_4=138 mm; Body_Top_Dia=36 mm  [stored 0.11811 ft]; Body_Top_Dia_2=30 mm  [stored 0.0984252 ft]; Body_With_Dia=123 mm; Body_With_Dia_1=245 mm; Body_With_Dia_2=245 mm; Bolt_support=754 mm; Bolt_support_2=377 mm; Bolt_support_Dia=30 mm  [stored 0.0984252 ft]; Bolt_support_lenght=195 mm; Bolt_support_lenght_2=205 mm; Bottom_profile=88 mm; D1=215 mm; D3=260 mm; DN=351 mm; Fillet_Length=15 mm  [stored 0.0492126 ft]; Fillet_Length_Ref=45 mm  [stored 0.147638 ft]; Flange_thickness=27 mm  [stored 0.0885827 ft]; H=945 mm; H3_Ref=930 mm; ID=175 mm; L=980 mm; L_Ref=464 mm; NV_Dia=200 mm; PG_Dia=117 mm; PG_Ref=163 mm; PG_depth=21 mm  [stored 0.0688976 ft]; PG_height=605 mm; PG_height_1=547 mm; PG_ref=185 mm; PR_1=53 mm; P_lenght=133 mm; Pilot_Dia_1=61 mm; Pilot_Dia_2=121 mm; Pilot_Dia_3=40 mm  [stored 0.131234 ft]; Pilot_Dia_4=20 mm  [stored 0.0656168 ft]; Pilot_Dia_5=13 mm; Pilot_top_1=575 mm; Pilot_top_ref=85 mm; Profile1_Height=395 mm; Profile1_Length=70 mm; Profile1_Length_2=47 mm; Profile_Dia=15 mm  [stored 0.0492126 ft]; Profile_Dia_2=15 mm  [stored 0.0492126 ft]; Profile_Dia_3=30 mm  [stored 0.0984252 ft]; Profile_Dia_Ref=8 mm  [stored 0.0262467 ft]; Profile_Dia_Ref_2=30 mm  [stored 0.0984252 ft]; Profile_height ref=40 mm  [stored 0.131234 ft]; T_Height=235 mm; T_Height_2=201 mm; T_Height_Ref_1=34 mm; T_Height_Ref_2=39 mm  [stored 0.127953 ft]; T_ref=541 mm; Top_Profile=452 mm; Top_Profile_Ref=457 mm; W=890 mm; W_Ref=869 mm
- 879-0350-00-14400319999_DN350_PN16: Body_Collar_Dia=89 mm; Body_Collar_Dia_2=61 mm; Body_Flange_Dia=280 mm; Body_Flange_Dia_2=306 mm; Body_Height_1=245 mm; Body_Height_2=123 mm; Body_Height_3=89 mm; Body_Height_4=138 mm; Body_Top_Dia=36 mm  [stored 0.11811 ft]; Body_Top_Dia_2=30 mm  [stored 0.0984252 ft]; Body_With_Dia=123 mm; Body_With_Dia_1=245 mm; Body_With_Dia_2=245 mm; Bolt_support=754 mm; Bolt_support_2=377 mm; Bolt_support_Dia=30 mm  [stored 0.0984252 ft]; Bolt_support_lenght=195 mm; Bolt_support_lenght_2=205 mm; Bottom_profile=88 mm; D1=215 mm; D3=260 mm; DN=351 mm; Fillet_Length=15 mm  [stored 0.0492126 ft]; Fillet_Length_Ref=45 mm  [stored 0.147638 ft]; Flange_thickness=27 mm  [stored 0.0885827 ft]; H=945 mm; H3_Ref=930 mm; ID=175 mm; L=980 mm; L_Ref=464 mm; NV_Dia=200 mm; PG_Dia=117 mm; PG_Ref=163 mm; PG_depth=21 mm  [stored 0.0688976 ft]; PG_height=605 mm; PG_height_1=547 mm; PG_ref=185 mm; PR_1=53 mm; P_lenght=139 mm; Pilot_Dia_1=63 mm; Pilot_Dia_2=126 mm; Pilot_Dia_3=42 mm  [stored 0.137795 ft]; Pilot_Dia_4=21 mm  [stored 0.0688976 ft]; Pilot_Dia_5=14 mm  [stored 0.0459318 ft]; Pilot_top_1=571 mm; Pilot_top_ref=89 mm; Profile1_Height=395 mm; Profile1_Length=70 mm; Profile1_Length_2=47 mm; Profile_Dia=15 mm  [stored 0.0492126 ft]; Profile_Dia_2=15 mm  [stored 0.0492126 ft]; Profile_Dia_3=30 mm  [stored 0.0984252 ft]; Profile_Dia_Ref=8 mm  [stored 0.0262467 ft]; Profile_Dia_Ref_2=30 mm  [stored 0.0984252 ft]; Profile_height ref=40 mm  [stored 0.131234 ft]; T_Height=235 mm; T_Height_2=201 mm; T_Height_Ref_1=34 mm; T_Height_Ref_2=39 mm  [stored 0.127953 ft]; T_ref=541 mm; Top_Profile=452 mm; Top_Profile_Ref=457 mm; W=890 mm; W_Ref=869 mm
- 879-0350-00-144003199A0_DN350_PN16: Body_Collar_Dia=89 mm; Body_Collar_Dia_2=61 mm; Body_Flange_Dia=280 mm; Body_Flange_Dia_2=306 mm; Body_Height_1=245 mm; Body_Height_2=123 mm; Body_Height_3=89 mm; Body_Height_4=138 mm; Body_Top_Dia=36 mm  [stored 0.11811 ft]; Body_Top_Dia_2=30 mm  [stored 0.0984252 ft]; Body_With_Dia=123 mm; Body_With_Dia_1=245 mm; Body_With_Dia_2=245 mm; Bolt_support=754 mm; Bolt_support_2=377 mm; Bolt_support_Dia=30 mm  [stored 0.0984252 ft]; Bolt_support_lenght=195 mm; Bolt_support_lenght_2=205 mm; Bottom_profile=88 mm; D1=215 mm; D3=260 mm; DN=351 mm; Fillet_Length=15 mm  [stored 0.0492126 ft]; Fillet_Length_Ref=45 mm  [stored 0.147638 ft]; Flange_thickness=27 mm  [stored 0.0885827 ft]; H=959 mm; H3_Ref=944 mm; ID=175 mm; L=980 mm; L_Ref=464 mm; NV_Dia=200 mm; PG_Dia=117 mm; PG_Ref=163 mm; PG_depth=21 mm  [stored 0.0688976 ft]; PG_height=608 mm; PG_height_1=550 mm; PG_ref=185 mm; PR_1=56 mm; P_lenght=139 mm; Pilot_Dia_1=63 mm; Pilot_Dia_2=126 mm; Pilot_Dia_3=42 mm  [stored 0.137795 ft]; Pilot_Dia_4=21 mm  [stored 0.0688976 ft]; Pilot_Dia_5=14 mm  [stored 0.0459318 ft]; Pilot_top_1=578 mm; Pilot_top_ref=96 mm; Profile1_Height=395 mm; Profile1_Length=70 mm; Profile1_Length_2=47 mm; Profile_Dia=15 mm  [stored 0.0492126 ft]; Profile_Dia_2=15 mm  [stored 0.0492126 ft]; Profile_Dia_3=30 mm  [stored 0.0984252 ft]; Profile_Dia_Ref=8 mm  [stored 0.0262467 ft]; Profile_Dia_Ref_2=30 mm  [stored 0.0984252 ft]; Profile_height ref=40 mm  [stored 0.131234 ft]; T_Height=249 mm; T_Height_2=213 mm; T_Height_Ref_1=36 mm  [stored 0.11811 ft]; T_Height_Ref_2=42 mm  [stored 0.137795 ft]; T_ref=548 mm; Top_Profile=452 mm; Top_Profile_Ref=457 mm; W=890 mm; W_Ref=869 mm
- 879-0350-00-14400329999_DN350_PN16: Body_Collar_Dia=89 mm; Body_Collar_Dia_2=61 mm; Body_Flange_Dia=280 mm; Body_Flange_Dia_2=306 mm; Body_Height_1=245 mm; Body_Height_2=123 mm; Body_Height_3=98 mm; Body_Height_4=138 mm; Body_Top_Dia=36 mm  [stored 0.11811 ft]; Body_Top_Dia_2=30 mm  [stored 0.0984252 ft]; Body_With_Dia=123 mm; Body_With_Dia_1=245 mm; Body_With_Dia_2=245 mm; Bolt_support=754 mm; Bolt_support_2=377 mm; Bolt_support_Dia=30 mm  [stored 0.0984252 ft]; Bolt_support_lenght=195 mm; Bolt_support_lenght_2=205 mm; Bottom_profile=88 mm; D1=215 mm; D3=260 mm; DN=351 mm; Fillet_Length=15 mm  [stored 0.0492126 ft]; Fillet_Length_Ref=45 mm  [stored 0.147638 ft]; Flange_thickness=27 mm  [stored 0.0885827 ft]; H=945 mm; H3_Ref=930 mm; ID=175 mm; L=980 mm; L_Ref=464 mm; NV_Dia=200 mm; PG_Dia=117 mm; PG_Ref=163 mm; PG_depth=21 mm  [stored 0.0688976 ft]; PG_height=605 mm; PG_height_1=547 mm; PG_ref=185 mm; PR_1=53 mm; P_lenght=133 mm; Pilot_Dia_1=61 mm; Pilot_Dia_2=121 mm; Pilot_Dia_3=40 mm  [stored 0.131234 ft]; Pilot_Dia_4=20 mm  [stored 0.0656168 ft]; Pilot_Dia_5=13 mm; Pilot_top_1=575 mm; Pilot_top_ref=85 mm; Profile1_Height=395 mm; Profile1_Length=70 mm; Profile1_Length_2=47 mm; Profile_Dia=15 mm  [stored 0.0492126 ft]; Profile_Dia_2=15 mm  [stored 0.0492126 ft]; Profile_Dia_3=30 mm  [stored 0.0984252 ft]; Profile_Dia_Ref=8 mm  [stored 0.0262467 ft]; Profile_Dia_Ref_2=30 mm  [stored 0.0984252 ft]; Profile_height ref=40 mm  [stored 0.131234 ft]; T_Height=235 mm; T_Height_2=201 mm; T_Height_Ref_1=34 mm; T_Height_Ref_2=39 mm  [stored 0.127953 ft]; T_ref=541 mm; Top_Profile=452 mm; Top_Profile_Ref=457 mm; W=890 mm; W_Ref=869 mm
- 879-0350-00-14400339999_DN350_PN16: Body_Collar_Dia=89 mm; Body_Collar_Dia_2=61 mm; Body_Flange_Dia=280 mm; Body_Flange_Dia_2=306 mm; Body_Height_1=245 mm; Body_Height_2=123 mm; Body_Height_3=98 mm; Body_Height_4=138 mm; Body_Top_Dia=36 mm  [stored 0.11811 ft]; Body_Top_Dia_2=30 mm  [stored 0.0984252 ft]; Body_With_Dia=123 mm; Body_With_Dia_1=245 mm; Body_With_Dia_2=245 mm; Bolt_support=754 mm; Bolt_support_2=377 mm; Bolt_support_Dia=30 mm  [stored 0.0984252 ft]; Bolt_support_lenght=195 mm; Bolt_support_lenght_2=205 mm; Bottom_profile=88 mm; D1=215 mm; D3=260 mm; DN=351 mm; Fillet_Length=15 mm  [stored 0.0492126 ft]; Fillet_Length_Ref=45 mm  [stored 0.147638 ft]; Flange_thickness=27 mm  [stored 0.0885827 ft]; H=945 mm; H3_Ref=930 mm; ID=175 mm; L=980 mm; L_Ref=464 mm; NV_Dia=200 mm; PG_Dia=117 mm; PG_Ref=163 mm; PG_depth=21 mm  [stored 0.0688976 ft]; PG_height=605 mm; PG_height_1=547 mm; PG_ref=185 mm; PR_1=53 mm; P_lenght=133 mm; Pilot_Dia_1=61 mm; Pilot_Dia_2=121 mm; Pilot_Dia_3=40 mm  [stored 0.131234 ft]; Pilot_Dia_4=20 mm  [stored 0.0656168 ft]; Pilot_Dia_5=13 mm; Pilot_top_1=575 mm; Pilot_top_ref=85 mm; Profile1_Height=395 mm; Profile1_Length=70 mm; Profile1_Length_2=47 mm; Profile_Dia=15 mm  [stored 0.0492126 ft]; Profile_Dia_2=15 mm  [stored 0.0492126 ft]; Profile_Dia_3=30 mm  [stored 0.0984252 ft]; Profile_Dia_Ref=8 mm  [stored 0.0262467 ft]; Profile_Dia_Ref_2=30 mm  [stored 0.0984252 ft]; Profile_height ref=40 mm  [stored 0.131234 ft]; T_Height=235 mm; T_Height_2=201 mm; T_Height_Ref_1=34 mm; T_Height_Ref_2=39 mm  [stored 0.127953 ft]; T_ref=541 mm; Top_Profile=452 mm; Top_Profile_Ref=457 mm; W=890 mm; W_Ref=869 mm
- 879-0400-00-04400309999_DN400_PN10: Body_Collar_Dia=100 mm; Body_Collar_Dia_2=69 mm; Body_Flange_Dia=314 mm; Body_Flange_Dia_2=344 mm; Body_Height_1=275 mm; Body_Height_2=138 mm; Body_Height_3=110 mm; Body_Height_4=153 mm; Body_Top_Dia=41 mm; Body_Top_Dia_2=34 mm; Body_With_Dia=138 mm; Body_With_Dia_1=275 mm; Body_With_Dia_2=275 mm; Bolt_support=846 mm; Bolt_support_2=423 mm; Bolt_support_Dia=40 mm  [stored 0.131234 ft]; Bolt_support_lenght=220 mm; Bolt_support_lenght_2=230 mm; Bottom_profile=100 mm; D1=240 mm; D3=283 mm; DN=400 mm; Fillet_Length=20 mm  [stored 0.0656168 ft]; Fillet_Length_Ref=60 mm; Flange_thickness=28 mm  [stored 0.0918635 ft]; H=1070 mm; H3_Ref=1050 mm; ID=200 mm; L=1100 mm; L_Ref=522 mm; NV_Dia=200 mm; PG_Dia=133 mm; PG_Ref=183 mm; PG_depth=28 mm  [stored 0.0918635 ft]; PG_height=690 mm; PG_height_1=623 mm; PG_ref=210 mm; PR_1=62 mm; P_lenght=152 mm; Pilot_Dia_1=69 mm; Pilot_Dia_2=138 mm; Pilot_Dia_3=46 mm  [stored 0.150919 ft]; Pilot_Dia_4=23 mm  [stored 0.0754593 ft]; Pilot_Dia_5=15 mm  [stored 0.0492126 ft]; Pilot_top_1=653 mm; Pilot_top_ref=105 mm; Profile1_Height=445 mm; Profile1_Length=76 mm; Profile1_Length_2=51 mm; Profile_Dia=20 mm  [stored 0.0656168 ft]; Profile_Dia_2=20 mm  [stored 0.0656168 ft]; Profile_Dia_3=40 mm  [stored 0.131234 ft]; Profile_Dia_Ref=10 mm  [stored 0.0328084 ft]; Profile_Dia_Ref_2=40 mm  [stored 0.131234 ft]; Profile_height ref=50 mm  [stored 0.164042 ft]; T_Height=273 mm; T_Height_2=234 mm; T_Height_Ref_1=39 mm  [stored 0.127953 ft]; T_Height_Ref_2=45 mm  [stored 0.147638 ft]; T_ref=618 mm; Top_Profile=508 mm; Top_Profile_Ref=513 mm; W=950 mm; W_Ref=922 mm
- 879-0400-00-04400319999_DN400_PN10: Body_Collar_Dia=100 mm; Body_Collar_Dia_2=69 mm; Body_Flange_Dia=314 mm; Body_Flange_Dia_2=344 mm; Body_Height_1=275 mm; Body_Height_2=138 mm; Body_Height_3=122 mm; Body_Height_4=153 mm; Body_Top_Dia=41 mm; Body_Top_Dia_2=34 mm; Body_With_Dia=138 mm; Body_With_Dia_1=275 mm; Body_With_Dia_2=275 mm; Bolt_support=846 mm; Bolt_support_2=423 mm; Bolt_support_Dia=40 mm  [stored 0.131234 ft]; Bolt_support_lenght=220 mm; Bolt_support_lenght_2=230 mm; Bottom_profile=100 mm; D1=240 mm; D3=283 mm; DN=400 mm; Fillet_Length=20 mm  [stored 0.0656168 ft]; Fillet_Length_Ref=60 mm; Flange_thickness=28 mm  [stored 0.0918635 ft]; H=1070 mm; H3_Ref=1050 mm; ID=200 mm; L=1100 mm; L_Ref=522 mm; NV_Dia=200 mm; PG_Dia=133 mm; PG_Ref=183 mm; PG_depth=28 mm  [stored 0.0918635 ft]; PG_height=690 mm; PG_height_1=623 mm; PG_ref=210 mm; PR_1=62 mm; P_lenght=152 mm; Pilot_Dia_1=69 mm; Pilot_Dia_2=138 mm; Pilot_Dia_3=46 mm  [stored 0.150919 ft]; Pilot_Dia_4=23 mm  [stored 0.0754593 ft]; Pilot_Dia_5=15 mm  [stored 0.0492126 ft]; Pilot_top_1=659 mm; Pilot_top_ref=99 mm; Profile1_Height=445 mm; Profile1_Length=76 mm; Profile1_Length_2=51 mm; Profile_Dia=20 mm  [stored 0.0656168 ft]; Profile_Dia_2=20 mm  [stored 0.0656168 ft]; Profile_Dia_3=40 mm  [stored 0.131234 ft]; Profile_Dia_Ref=10 mm  [stored 0.0328084 ft]; Profile_Dia_Ref_2=40 mm  [stored 0.131234 ft]; Profile_height ref=50 mm  [stored 0.164042 ft]; T_Height=273 mm; T_Height_2=234 mm; T_Height_Ref_1=39 mm  [stored 0.127953 ft]; T_Height_Ref_2=45 mm  [stored 0.147638 ft]; T_ref=618 mm; Top_Profile=508 mm; Top_Profile_Ref=513 mm; W=950 mm; W_Ref=922 mm
- 879-0400-00-044003199A0_DN400_PN10: Body_Collar_Dia=100 mm; Body_Collar_Dia_2=69 mm; Body_Flange_Dia=314 mm; Body_Flange_Dia_2=344 mm; Body_Height_1=275 mm; Body_Height_2=138 mm; Body_Height_3=100 mm; Body_Height_4=153 mm; Body_Top_Dia=41 mm; Body_Top_Dia_2=34 mm; Body_With_Dia=138 mm; Body_With_Dia_1=275 mm; Body_With_Dia_2=275 mm; Bolt_support=846 mm; Bolt_support_2=423 mm; Bolt_support_Dia=40 mm  [stored 0.131234 ft]; Bolt_support_lenght=220 mm; Bolt_support_lenght_2=230 mm; Bottom_profile=100 mm; D1=240 mm; D3=283 mm; DN=400 mm; Fillet_Length=20 mm  [stored 0.0656168 ft]; Fillet_Length_Ref=60 mm; Flange_thickness=28 mm  [stored 0.0918635 ft]; H=1159 mm; H3_Ref=1139 mm; ID=200 mm; L=1100 mm; L_Ref=522 mm; NV_Dia=200 mm; PG_Dia=133 mm; PG_Ref=183 mm; PG_depth=28 mm  [stored 0.0918635 ft]; PG_height=710 mm; PG_height_1=643 mm; PG_ref=210 mm; PR_1=82 mm; P_lenght=156 mm; Pilot_Dia_1=71 mm; Pilot_Dia_2=142 mm; Pilot_Dia_3=47 mm; Pilot_Dia_4=24 mm  [stored 0.0787402 ft]; Pilot_Dia_5=16 mm  [stored 0.0524934 ft]; Pilot_top_1=692 mm; Pilot_top_ref=155 mm; Profile1_Height=445 mm; Profile1_Length=76 mm; Profile1_Length_2=51 mm; Profile_Dia=20 mm  [stored 0.0656168 ft]; Profile_Dia_2=20 mm  [stored 0.0656168 ft]; Profile_Dia_3=40 mm  [stored 0.131234 ft]; Profile_Dia_Ref=10 mm  [stored 0.0328084 ft]; Profile_Dia_Ref_2=40 mm  [stored 0.131234 ft]; Profile_height ref=50 mm  [stored 0.164042 ft]; T_Height=362 mm; T_Height_2=310 mm; T_Height_Ref_1=52 mm; T_Height_Ref_2=60 mm; T_ref=659 mm; Top_Profile=508 mm; Top_Profile_Ref=513 mm; W=950 mm; W_Ref=922 mm
- 879-0400-00-04400329999_DN400_PN10: Body_Collar_Dia=100 mm; Body_Collar_Dia_2=69 mm; Body_Flange_Dia=314 mm; Body_Flange_Dia_2=344 mm; Body_Height_1=275 mm; Body_Height_2=138 mm; Body_Height_3=110 mm; Body_Height_4=153 mm; Body_Top_Dia=41 mm; Body_Top_Dia_2=34 mm; Body_With_Dia=138 mm; Body_With_Dia_1=275 mm; Body_With_Dia_2=275 mm; Bolt_support=846 mm; Bolt_support_2=423 mm; Bolt_support_Dia=40 mm  [stored 0.131234 ft]; Bolt_support_lenght=220 mm; Bolt_support_lenght_2=230 mm; Bottom_profile=100 mm; D1=240 mm; D3=283 mm; DN=400 mm; Fillet_Length=20 mm  [stored 0.0656168 ft]; Fillet_Length_Ref=60 mm; Flange_thickness=28 mm  [stored 0.0918635 ft]; H=1070 mm; H3_Ref=1050 mm; ID=200 mm; L=1100 mm; L_Ref=522 mm; NV_Dia=200 mm; PG_Dia=133 mm; PG_Ref=183 mm; PG_depth=28 mm  [stored 0.0918635 ft]; PG_height=690 mm; PG_height_1=623 mm; PG_ref=210 mm; PR_1=62 mm; P_lenght=156 mm; Pilot_Dia_1=71 mm; Pilot_Dia_2=142 mm; Pilot_Dia_3=47 mm; Pilot_Dia_4=24 mm  [stored 0.0787402 ft]; Pilot_Dia_5=16 mm  [stored 0.0524934 ft]; Pilot_top_1=653 mm; Pilot_top_ref=105 mm; Profile1_Height=445 mm; Profile1_Length=76 mm; Profile1_Length_2=51 mm; Profile_Dia=20 mm  [stored 0.0656168 ft]; Profile_Dia_2=20 mm  [stored 0.0656168 ft]; Profile_Dia_3=40 mm  [stored 0.131234 ft]; Profile_Dia_Ref=10 mm  [stored 0.0328084 ft]; Profile_Dia_Ref_2=40 mm  [stored 0.131234 ft]; Profile_height ref=50 mm  [stored 0.164042 ft]; T_Height=273 mm; T_Height_2=234 mm; T_Height_Ref_1=39 mm  [stored 0.127953 ft]; T_Height_Ref_2=45 mm  [stored 0.147638 ft]; T_ref=618 mm; Top_Profile=508 mm; Top_Profile_Ref=513 mm; W=950 mm; W_Ref=922 mm
- 879-0400-00-04400339999_DN400_PN10: Body_Collar_Dia=100 mm; Body_Collar_Dia_2=69 mm; Body_Flange_Dia=314 mm; Body_Flange_Dia_2=344 mm; Body_Height_1=275 mm; Body_Height_2=138 mm; Body_Height_3=110 mm; Body_Height_4=153 mm; Body_Top_Dia=41 mm; Body_Top_Dia_2=34 mm; Body_With_Dia=138 mm; Body_With_Dia_1=275 mm; Body_With_Dia_2=275 mm; Bolt_support=846 mm; Bolt_support_2=423 mm; Bolt_support_Dia=40 mm  [stored 0.131234 ft]; Bolt_support_lenght=220 mm; Bolt_support_lenght_2=230 mm; Bottom_profile=100 mm; D1=240 mm; D3=283 mm; DN=400 mm; Fillet_Length=20 mm  [stored 0.0656168 ft]; Fillet_Length_Ref=60 mm; Flange_thickness=28 mm  [stored 0.0918635 ft]; H=1070 mm; H3_Ref=1050 mm; ID=200 mm; L=1100 mm; L_Ref=522 mm; NV_Dia=200 mm; PG_Dia=133 mm; PG_Ref=183 mm; PG_depth=28 mm  [stored 0.0918635 ft]; PG_height=690 mm; PG_height_1=623 mm; PG_ref=210 mm; PR_1=62 mm; P_lenght=152 mm; Pilot_Dia_1=69 mm; Pilot_Dia_2=138 mm; Pilot_Dia_3=46 mm  [stored 0.150919 ft]; Pilot_Dia_4=23 mm  [stored 0.0754593 ft]; Pilot_Dia_5=15 mm  [stored 0.0492126 ft]; Pilot_top_1=653 mm; Pilot_top_ref=105 mm; Profile1_Height=445 mm; Profile1_Length=76 mm; Profile1_Length_2=51 mm; Profile_Dia=20 mm  [stored 0.0656168 ft]; Profile_Dia_2=20 mm  [stored 0.0656168 ft]; Profile_Dia_3=40 mm  [stored 0.131234 ft]; Profile_Dia_Ref=10 mm  [stored 0.0328084 ft]; Profile_Dia_Ref_2=40 mm  [stored 0.131234 ft]; Profile_height ref=50 mm  [stored 0.164042 ft]; T_Height=273 mm; T_Height_2=234 mm; T_Height_Ref_1=39 mm  [stored 0.127953 ft]; T_Height_Ref_2=45 mm  [stored 0.147638 ft]; T_ref=618 mm; Top_Profile=508 mm; Top_Profile_Ref=513 mm; W=950 mm; W_Ref=922 mm
- 879-0400-00-14400309999_DN400_PN16: Body_Collar_Dia=100 mm; Body_Collar_Dia_2=69 mm; Body_Flange_Dia=314 mm; Body_Flange_Dia_2=344 mm; Body_Height_1=275 mm; Body_Height_2=138 mm; Body_Height_3=122 mm; Body_Height_4=153 mm; Body_Top_Dia=41 mm; Body_Top_Dia_2=34 mm; Body_With_Dia=138 mm; Body_With_Dia_1=275 mm; Body_With_Dia_2=275 mm; Bolt_support=846 mm; Bolt_support_2=423 mm; Bolt_support_Dia=40 mm  [stored 0.131234 ft]; Bolt_support_lenght=220 mm; Bolt_support_lenght_2=230 mm; Bottom_profile=100 mm; D1=240 mm; D3=290 mm; DN=401 mm; Fillet_Length=20 mm  [stored 0.0656168 ft]; Fillet_Length_Ref=60 mm; Flange_thickness=28 mm  [stored 0.0918635 ft]; H=1070 mm; H3_Ref=1050 mm; ID=200 mm; L=1100 mm; L_Ref=522 mm; NV_Dia=200 mm; PG_Dia=134 mm; PG_Ref=183 mm; PG_depth=28 mm  [stored 0.0918635 ft]; PG_height=688 mm; PG_height_1=622 mm; PG_ref=210 mm; PR_1=60 mm; P_lenght=152 mm; Pilot_Dia_1=69 mm; Pilot_Dia_2=138 mm; Pilot_Dia_3=46 mm  [stored 0.150919 ft]; Pilot_Dia_4=23 mm  [stored 0.0754593 ft]; Pilot_Dia_5=15 mm  [stored 0.0492126 ft]; Pilot_top_1=655 mm; Pilot_top_ref=95 mm; Profile1_Height=445 mm; Profile1_Length=78 mm; Profile1_Length_2=52 mm; Profile_Dia=20 mm  [stored 0.0656168 ft]; Profile_Dia_2=20 mm  [stored 0.0656168 ft]; Profile_Dia_3=40 mm  [stored 0.131234 ft]; Profile_Dia_Ref=10 mm  [stored 0.0328084 ft]; Profile_Dia_Ref_2=40 mm  [stored 0.131234 ft]; Profile_height ref=50 mm  [stored 0.164042 ft]; T_Height=265 mm; T_Height_2=227 mm; T_Height_Ref_1=38 mm  [stored 0.124672 ft]; T_Height_Ref_2=44 mm; T_ref=615 mm; Top_Profile=508 mm; Top_Profile_Ref=513 mm; W=950 mm; W_Ref=922 mm
- 879-0400-00-14400319999_DN400_PN16: Body_Collar_Dia=100 mm; Body_Collar_Dia_2=69 mm; Body_Flange_Dia=314 mm; Body_Flange_Dia_2=344 mm; Body_Height_1=275 mm; Body_Height_2=138 mm; Body_Height_3=100 mm; Body_Height_4=153 mm; Body_Top_Dia=41 mm; Body_Top_Dia_2=34 mm; Body_With_Dia=138 mm; Body_With_Dia_1=275 mm; Body_With_Dia_2=275 mm; Bolt_support=846 mm; Bolt_support_2=423 mm; Bolt_support_Dia=40 mm  [stored 0.131234 ft]; Bolt_support_lenght=220 mm; Bolt_support_lenght_2=230 mm; Bottom_profile=100 mm; D1=240 mm; D3=290 mm; DN=401 mm; Fillet_Length=20 mm  [stored 0.0656168 ft]; Fillet_Length_Ref=60 mm; Flange_thickness=28 mm  [stored 0.0918635 ft]; H=1070 mm; H3_Ref=1050 mm; ID=200 mm; L=1100 mm; L_Ref=522 mm; NV_Dia=200 mm; PG_Dia=134 mm; PG_Ref=183 mm; PG_depth=28 mm  [stored 0.0918635 ft]; PG_height=688 mm; PG_height_1=622 mm; PG_ref=210 mm; PR_1=60 mm; P_lenght=156 mm; Pilot_Dia_1=71 mm; Pilot_Dia_2=142 mm; Pilot_Dia_3=47 mm; Pilot_Dia_4=24 mm  [stored 0.0787402 ft]; Pilot_Dia_5=16 mm  [stored 0.0524934 ft]; Pilot_top_1=644 mm; Pilot_top_ref=106 mm; Profile1_Height=445 mm; Profile1_Length=78 mm; Profile1_Length_2=52 mm; Profile_Dia=20 mm  [stored 0.0656168 ft]; Profile_Dia_2=20 mm  [stored 0.0656168 ft]; Profile_Dia_3=40 mm  [stored 0.131234 ft]; Profile_Dia_Ref=10 mm  [stored 0.0328084 ft]; Profile_Dia_Ref_2=40 mm  [stored 0.131234 ft]; Profile_height ref=50 mm  [stored 0.164042 ft]; T_Height=265 mm; T_Height_2=227 mm; T_Height_Ref_1=38 mm  [stored 0.124672 ft]; T_Height_Ref_2=44 mm; T_ref=615 mm; Top_Profile=508 mm; Top_Profile_Ref=513 mm; W=950 mm; W_Ref=922 mm
- 879-0400-00-144003199A0_DN400_PN16: Body_Collar_Dia=100 mm; Body_Collar_Dia_2=69 mm; Body_Flange_Dia=314 mm; Body_Flange_Dia_2=344 mm; Body_Height_1=275 mm; Body_Height_2=138 mm; Body_Height_3=110 mm; Body_Height_4=153 mm; Body_Top_Dia=41 mm; Body_Top_Dia_2=34 mm; Body_With_Dia=138 mm; Body_With_Dia_1=275 mm; Body_With_Dia_2=275 mm; Bolt_support=846 mm; Bolt_support_2=423 mm; Bolt_support_Dia=40 mm  [stored 0.131234 ft]; Bolt_support_lenght=220 mm; Bolt_support_lenght_2=230 mm; Bottom_profile=100 mm; D1=240 mm; D3=290 mm; DN=401 mm; Fillet_Length=20 mm  [stored 0.0656168 ft]; Fillet_Length_Ref=60 mm; Flange_thickness=28 mm  [stored 0.0918635 ft]; H=1159 mm; H3_Ref=1139 mm; ID=200 mm; L=1100 mm; L_Ref=522 mm; NV_Dia=200 mm; PG_Dia=134 mm; PG_Ref=183 mm; PG_depth=28 mm  [stored 0.0918635 ft]; PG_height=709 mm; PG_height_1=642 mm; PG_ref=210 mm; PR_1=80 mm; P_lenght=156 mm; Pilot_Dia_1=71 mm; Pilot_Dia_2=142 mm; Pilot_Dia_3=47 mm; Pilot_Dia_4=24 mm  [stored 0.0787402 ft]; Pilot_Dia_5=16 mm  [stored 0.0524934 ft]; Pilot_top_1=693 mm; Pilot_top_ref=146 mm; Profile1_Height=445 mm; Profile1_Length=78 mm; Profile1_Length_2=52 mm; Profile_Dia=20 mm  [stored 0.0656168 ft]; Profile_Dia_2=20 mm  [stored 0.0656168 ft]; Profile_Dia_3=40 mm  [stored 0.131234 ft]; Profile_Dia_Ref=10 mm  [stored 0.0328084 ft]; Profile_Dia_Ref_2=40 mm  [stored 0.131234 ft]; Profile_height ref=50 mm  [stored 0.164042 ft]; T_Height=354 mm; T_Height_2=303 mm; T_Height_Ref_1=51 mm; T_Height_Ref_2=59 mm; T_ref=655 mm; Top_Profile=508 mm; Top_Profile_Ref=513 mm; W=950 mm; W_Ref=922 mm
- 879-0400-00-14400329999_DN400_PN16: Body_Collar_Dia=100 mm; Body_Collar_Dia_2=69 mm; Body_Flange_Dia=314 mm; Body_Flange_Dia_2=344 mm; Body_Height_1=275 mm; Body_Height_2=138 mm; Body_Height_3=110 mm; Body_Height_4=153 mm; Body_Top_Dia=41 mm; Body_Top_Dia_2=34 mm; Body_With_Dia=138 mm; Body_With_Dia_1=275 mm; Body_With_Dia_2=275 mm; Bolt_support=846 mm; Bolt_support_2=423 mm; Bolt_support_Dia=40 mm  [stored 0.131234 ft]; Bolt_support_lenght=220 mm; Bolt_support_lenght_2=230 mm; Bottom_profile=100 mm; D1=240 mm; D3=290 mm; DN=401 mm; Fillet_Length=20 mm  [stored 0.0656168 ft]; Fillet_Length_Ref=60 mm; Flange_thickness=28 mm  [stored 0.0918635 ft]; H=1070 mm; H3_Ref=1050 mm; ID=200 mm; L=1100 mm; L_Ref=522 mm; NV_Dia=200 mm; PG_Dia=134 mm; PG_Ref=183 mm; PG_depth=28 mm  [stored 0.0918635 ft]; PG_height=689 mm; PG_height_1=622 mm; PG_ref=210 mm; PR_1=60 mm; P_lenght=152 mm; Pilot_Dia_1=69 mm; Pilot_Dia_2=138 mm; Pilot_Dia_3=46 mm  [stored 0.150919 ft]; Pilot_Dia_4=23 mm  [stored 0.0754593 ft]; Pilot_Dia_5=15 mm  [stored 0.0492126 ft]; Pilot_top_1=649 mm; Pilot_top_ref=101 mm; Profile1_Height=445 mm; Profile1_Length=78 mm; Profile1_Length_2=52 mm; Profile_Dia=20 mm  [stored 0.0656168 ft]; Profile_Dia_2=20 mm  [stored 0.0656168 ft]; Profile_Dia_3=40 mm  [stored 0.131234 ft]; Profile_Dia_Ref=10 mm  [stored 0.0328084 ft]; Profile_Dia_Ref_2=40 mm  [stored 0.131234 ft]; Profile_height ref=50 mm  [stored 0.164042 ft]; T_Height=265 mm; T_Height_2=227 mm; T_Height_Ref_1=38 mm  [stored 0.124672 ft]; T_Height_Ref_2=44 mm; T_ref=615 mm; Top_Profile=508 mm; Top_Profile_Ref=513 mm; W=950 mm; W_Ref=922 mm
- 879-0400-00-14400339999_DN400_PN16: Body_Collar_Dia=100 mm; Body_Collar_Dia_2=69 mm; Body_Flange_Dia=314 mm; Body_Flange_Dia_2=344 mm; Body_Height_1=275 mm; Body_Height_2=138 mm; Body_Height_3=122 mm; Body_Height_4=153 mm; Body_Top_Dia=41 mm; Body_Top_Dia_2=34 mm; Body_With_Dia=138 mm; Body_With_Dia_1=275 mm; Body_With_Dia_2=275 mm; Bolt_support=846 mm; Bolt_support_2=423 mm; Bolt_support_Dia=40 mm  [stored 0.131234 ft]; Bolt_support_lenght=220 mm; Bolt_support_lenght_2=230 mm; Bottom_profile=100 mm; D1=240 mm; D3=290 mm; DN=401 mm; Fillet_Length=20 mm  [stored 0.0656168 ft]; Fillet_Length_Ref=60 mm; Flange_thickness=28 mm  [stored 0.0918635 ft]; H=1070 mm; H3_Ref=1050 mm; ID=200 mm; L=1100 mm; L_Ref=522 mm; NV_Dia=200 mm; PG_Dia=134 mm; PG_Ref=183 mm; PG_depth=28 mm  [stored 0.0918635 ft]; PG_height=689 mm; PG_height_1=622 mm; PG_ref=210 mm; PR_1=60 mm; P_lenght=152 mm; Pilot_Dia_1=69 mm; Pilot_Dia_2=138 mm; Pilot_Dia_3=46 mm  [stored 0.150919 ft]; Pilot_Dia_4=23 mm  [stored 0.0754593 ft]; Pilot_Dia_5=15 mm  [stored 0.0492126 ft]; Pilot_top_1=655 mm; Pilot_top_ref=95 mm; Profile1_Height=445 mm; Profile1_Length=78 mm; Profile1_Length_2=52 mm; Profile_Dia=20 mm  [stored 0.0656168 ft]; Profile_Dia_2=20 mm  [stored 0.0656168 ft]; Profile_Dia_3=40 mm  [stored 0.131234 ft]; Profile_Dia_Ref=10 mm  [stored 0.0328084 ft]; Profile_Dia_Ref_2=40 mm  [stored 0.131234 ft]; Profile_height ref=50 mm  [stored 0.164042 ft]; T_Height=265 mm; T_Height_2=227 mm; T_Height_Ref_1=38 mm  [stored 0.124672 ft]; T_Height_Ref_2=44 mm; T_ref=615 mm; Top_Profile=508 mm; Top_Profile_Ref=513 mm; W=950 mm; W_Ref=922 mm
- 879-0450-00-04400309999_DN450_PN10: Body_Collar_Dia=109 mm; Body_Collar_Dia_2=75 mm; Body_Flange_Dia=343 mm; Body_Flange_Dia_2=375 mm; Body_Height_1=300 mm; Body_Height_2=150 mm; Body_Height_3=120 mm; Body_Height_4=165 mm; Body_Top_Dia=44 mm; Body_Top_Dia_2=37 mm; Body_With_Dia=150 mm; Body_With_Dia_1=300 mm; Body_With_Dia_2=300 mm; Bolt_support=923 mm; Bolt_support_2=462 mm; Bolt_support_Dia=40 mm  [stored 0.131234 ft]; Bolt_support_lenght=245 mm; Bolt_support_lenght_2=255 mm; Bottom_profile=113 mm; D1=265 mm; D3=308 mm; DN=450 mm; Fillet_Length=20 mm  [stored 0.0656168 ft]; Fillet_Length_Ref=60 mm; Flange_thickness=30 mm  [stored 0.0984252 ft]; H=1130 mm; H3_Ref=1110 mm; ID=225 mm; L=1200 mm; L_Ref=570 mm; NV_Dia=200 mm; PG_Dia=150 mm; PG_Ref=200 mm; PG_depth=28 mm  [stored 0.0918635 ft]; PG_height=737 mm; PG_height_1=662 mm; PG_ref=235 mm; PR_1=63 mm; P_lenght=166 mm; Pilot_Dia_1=76 mm; Pilot_Dia_2=151 mm; Pilot_Dia_3=50 mm  [stored 0.164042 ft]; Pilot_Dia_4=25 mm  [stored 0.082021 ft]; Pilot_Dia_5=17 mm; Pilot_top_1=694 mm; Pilot_top_ref=99 mm; Profile1_Height=474 mm; Profile1_Length=83 mm; Profile1_Length_2=55 mm; Profile_Dia=20 mm  [stored 0.0656168 ft]; Profile_Dia_2=20 mm  [stored 0.0656168 ft]; Profile_Dia_3=40 mm  [stored 0.131234 ft]; Profile_Dia_Ref=10 mm  [stored 0.0328084 ft]; Profile_Dia_Ref_2=40 mm  [stored 0.131234 ft]; Profile_height ref=50 mm  [stored 0.164042 ft]; T_Height=279 mm; T_Height_2=239 mm; T_Height_Ref_1=40 mm  [stored 0.131234 ft]; T_Height_Ref_2=46 mm  [stored 0.150919 ft]; T_ref=650 mm; Top_Profile=554 mm; Top_Profile_Ref=559 mm; W=1010 mm; W_Ref=982 mm
- 879-0450-00-04400319999_DN450_PN10: Body_Collar_Dia=109 mm; Body_Collar_Dia_2=75 mm; Body_Flange_Dia=343 mm; Body_Flange_Dia_2=375 mm; Body_Height_1=300 mm; Body_Height_2=150 mm; Body_Height_3=120 mm; Body_Height_4=165 mm; Body_Top_Dia=44 mm; Body_Top_Dia_2=37 mm; Body_With_Dia=150 mm; Body_With_Dia_1=300 mm; Body_With_Dia_2=300 mm; Bolt_support=923 mm; Bolt_support_2=462 mm; Bolt_support_Dia=40 mm  [stored 0.131234 ft]; Bolt_support_lenght=245 mm; Bolt_support_lenght_2=255 mm; Bottom_profile=113 mm; D1=265 mm; D3=308 mm; DN=450 mm; Fillet_Length=20 mm  [stored 0.0656168 ft]; Fillet_Length_Ref=60 mm; Flange_thickness=30 mm  [stored 0.0984252 ft]; H=1130 mm; H3_Ref=1110 mm; ID=225 mm; L=1200 mm; L_Ref=570 mm; NV_Dia=200 mm; PG_Dia=150 mm; PG_Ref=200 mm; PG_depth=28 mm  [stored 0.0918635 ft]; PG_height=754 mm; PG_height_1=679 mm; PG_ref=235 mm; PR_1=58 mm; P_lenght=166 mm; Pilot_Dia_1=76 mm; Pilot_Dia_2=151 mm; Pilot_Dia_3=50 mm  [stored 0.164042 ft]; Pilot_Dia_4=25 mm  [stored 0.082021 ft]; Pilot_Dia_5=17 mm; Pilot_top_1=694 mm; Pilot_top_ref=99 mm; Profile1_Height=496 mm; Profile1_Length=83 mm; Profile1_Length_2=55 mm; Profile_Dia=20 mm  [stored 0.0656168 ft]; Profile_Dia_2=20 mm  [stored 0.0656168 ft]; Profile_Dia_3=40 mm  [stored 0.131234 ft]; Profile_Dia_Ref=10 mm  [stored 0.0328084 ft]; Profile_Dia_Ref_2=40 mm  [stored 0.131234 ft]; Profile_height ref=50 mm  [stored 0.164042 ft]; T_Height=257 mm; T_Height_2=220 mm; T_Height_Ref_1=37 mm; T_Height_Ref_2=43 mm; T_ref=662 mm; Top_Profile=554 mm; Top_Profile_Ref=559 mm; W=1010 mm; W_Ref=982 mm
- 879-0450-00-044003199A0_DN450_PN10: Body_Collar_Dia=109 mm; Body_Collar_Dia_2=75 mm; Body_Flange_Dia=343 mm; Body_Flange_Dia_2=375 mm; Body_Height_1=300 mm; Body_Height_2=150 mm; Body_Height_3=120 mm; Body_Height_4=165 mm; Body_Top_Dia=44 mm; Body_Top_Dia_2=37 mm; Body_With_Dia=150 mm; Body_With_Dia_1=300 mm; Body_With_Dia_2=300 mm; Bolt_support=923 mm; Bolt_support_2=462 mm; Bolt_support_Dia=40 mm  [stored 0.131234 ft]; Bolt_support_lenght=245 mm; Bolt_support_lenght_2=255 mm; Bottom_profile=113 mm; D1=265 mm; D3=308 mm; DN=450 mm; Fillet_Length=20 mm  [stored 0.0656168 ft]; Fillet_Length_Ref=60 mm; Flange_thickness=30 mm  [stored 0.0984252 ft]; H=1220 mm; H3_Ref=1200 mm; ID=225 mm; L=1200 mm; L_Ref=570 mm; NV_Dia=200 mm; PG_Dia=150 mm; PG_Ref=200 mm; PG_depth=28 mm  [stored 0.0918635 ft]; PG_height=774 mm; PG_height_1=699 mm; PG_ref=235 mm; PR_1=79 mm; P_lenght=174 mm; Pilot_Dia_1=79 mm; Pilot_Dia_2=158 mm; Pilot_Dia_3=53 mm; Pilot_Dia_4=26 mm; Pilot_Dia_5=18 mm; Pilot_top_1=739 mm; Pilot_top_ref=144 mm; Profile1_Height=495 mm; Profile1_Length=83 mm; Profile1_Length_2=55 mm; Profile_Dia=20 mm  [stored 0.0656168 ft]; Profile_Dia_2=20 mm  [stored 0.0656168 ft]; Profile_Dia_3=40 mm  [stored 0.131234 ft]; Profile_Dia_Ref=10 mm  [stored 0.0328084 ft]; Profile_Dia_Ref_2=40 mm  [stored 0.131234 ft]; Profile_height ref=50 mm  [stored 0.164042 ft]; T_Height=348 mm; T_Height_2=298 mm; T_Height_Ref_1=50 mm  [stored 0.164042 ft]; T_Height_Ref_2=58 mm; T_ref=702 mm; Top_Profile=554 mm; Top_Profile_Ref=559 mm; W=1010 mm; W_Ref=982 mm
- 879-0450-00-04400329999_DN450_PN10: Body_Collar_Dia=109 mm; Body_Collar_Dia_2=75 mm; Body_Flange_Dia=343 mm; Body_Flange_Dia_2=375 mm; Body_Height_1=300 mm; Body_Height_2=150 mm; Body_Height_3=120 mm; Body_Height_4=165 mm; Body_Top_Dia=44 mm; Body_Top_Dia_2=37 mm; Body_With_Dia=150 mm; Body_With_Dia_1=300 mm; Body_With_Dia_2=300 mm; Bolt_support=923 mm; Bolt_support_2=462 mm; Bolt_support_Dia=40 mm  [stored 0.131234 ft]; Bolt_support_lenght=245 mm; Bolt_support_lenght_2=255 mm; Bottom_profile=113 mm; D1=265 mm; D3=308 mm; DN=450 mm; Fillet_Length=20 mm  [stored 0.0656168 ft]; Fillet_Length_Ref=60 mm; Flange_thickness=30 mm  [stored 0.0984252 ft]; H=1130 mm; H3_Ref=1110 mm; ID=225 mm; L=1200 mm; L_Ref=570 mm; NV_Dia=200 mm; PG_Dia=150 mm; PG_Ref=200 mm; PG_depth=28 mm  [stored 0.0918635 ft]; PG_height=754 mm; PG_height_1=679 mm; PG_ref=235 mm; PR_1=58 mm; P_lenght=174 mm; Pilot_Dia_1=79 mm; Pilot_Dia_2=158 mm; Pilot_Dia_3=53 mm; Pilot_Dia_4=26 mm; Pilot_Dia_5=18 mm; Pilot_top_1=694 mm; Pilot_top_ref=99 mm; Profile1_Height=496 mm; Profile1_Length=83 mm; Profile1_Length_2=55 mm; Profile_Dia=20 mm  [stored 0.0656168 ft]; Profile_Dia_2=20 mm  [stored 0.0656168 ft]; Profile_Dia_3=40 mm  [stored 0.131234 ft]; Profile_Dia_Ref=10 mm  [stored 0.0328084 ft]; Profile_Dia_Ref_2=40 mm  [stored 0.131234 ft]; Profile_height ref=50 mm  [stored 0.164042 ft]; T_Height=257 mm; T_Height_2=220 mm; T_Height_Ref_1=37 mm; T_Height_Ref_2=43 mm; T_ref=662 mm; Top_Profile=554 mm; Top_Profile_Ref=559 mm; W=1010 mm; W_Ref=982 mm
- 879-0450-00-04400339999_DN450_PN10: Body_Collar_Dia=109 mm; Body_Collar_Dia_2=75 mm; Body_Flange_Dia=343 mm; Body_Flange_Dia_2=375 mm; Body_Height_1=300 mm; Body_Height_2=150 mm; Body_Height_3=120 mm; Body_Height_4=165 mm; Body_Top_Dia=44 mm; Body_Top_Dia_2=37 mm; Body_With_Dia=150 mm; Body_With_Dia_1=300 mm; Body_With_Dia_2=300 mm; Bolt_support=923 mm; Bolt_support_2=462 mm; Bolt_support_Dia=40 mm  [stored 0.131234 ft]; Bolt_support_lenght=245 mm; Bolt_support_lenght_2=255 mm; Bottom_profile=113 mm; D1=265 mm; D3=308 mm; DN=450 mm; Fillet_Length=20 mm  [stored 0.0656168 ft]; Fillet_Length_Ref=60 mm; Flange_thickness=30 mm  [stored 0.0984252 ft]; H=1130 mm; H3_Ref=1110 mm; ID=225 mm; L=1200 mm; L_Ref=570 mm; NV_Dia=200 mm; PG_Dia=150 mm; PG_Ref=200 mm; PG_depth=28 mm  [stored 0.0918635 ft]; PG_height=737 mm; PG_height_1=662 mm; PG_ref=235 mm; PR_1=63 mm; P_lenght=166 mm; Pilot_Dia_1=76 mm; Pilot_Dia_2=151 mm; Pilot_Dia_3=50 mm  [stored 0.164042 ft]; Pilot_Dia_4=25 mm  [stored 0.082021 ft]; Pilot_Dia_5=17 mm; Pilot_top_1=694 mm; Pilot_top_ref=99 mm; Profile1_Height=474 mm; Profile1_Length=83 mm; Profile1_Length_2=55 mm; Profile_Dia=20 mm  [stored 0.0656168 ft]; Profile_Dia_2=20 mm  [stored 0.0656168 ft]; Profile_Dia_3=40 mm  [stored 0.131234 ft]; Profile_Dia_Ref=10 mm  [stored 0.0328084 ft]; Profile_Dia_Ref_2=40 mm  [stored 0.131234 ft]; Profile_height ref=50 mm  [stored 0.164042 ft]; T_Height=279 mm; T_Height_2=239 mm; T_Height_Ref_1=40 mm  [stored 0.131234 ft]; T_Height_Ref_2=46 mm  [stored 0.150919 ft]; T_ref=650 mm; Top_Profile=554 mm; Top_Profile_Ref=559 mm; W=1010 mm; W_Ref=982 mm
- 879-0450-00-14400309999_DN450_PN16: Body_Collar_Dia=109 mm; Body_Collar_Dia_2=75 mm; Body_Flange_Dia=343 mm; Body_Flange_Dia_2=375 mm; Body_Height_1=300 mm; Body_Height_2=150 mm; Body_Height_3=120 mm; Body_Height_4=165 mm; Body_Top_Dia=44 mm; Body_Top_Dia_2=37 mm; Body_With_Dia=150 mm; Body_With_Dia_1=300 mm; Body_With_Dia_2=300 mm; Bolt_support=923 mm; Bolt_support_2=462 mm; Bolt_support_Dia=40 mm  [stored 0.131234 ft]; Bolt_support_lenght=245 mm; Bolt_support_lenght_2=255 mm; Bottom_profile=113 mm; D1=274 mm; D3=320 mm; DN=451 mm; Fillet_Length=20 mm  [stored 0.0656168 ft]; Fillet_Length_Ref=60 mm; Flange_thickness=30 mm  [stored 0.0984252 ft]; H=1130 mm; H3_Ref=1110 mm; ID=225 mm; L=1200 mm; L_Ref=570 mm; NV_Dia=200 mm; PG_Dia=150 mm; PG_Ref=200 mm; PG_depth=28 mm  [stored 0.0918635 ft]; PG_height=751 mm; PG_height_1=676 mm; PG_ref=235 mm; PR_1=55 mm; P_lenght=166 mm; Pilot_Dia_1=76 mm; Pilot_Dia_2=151 mm; Pilot_Dia_3=50 mm  [stored 0.164042 ft]; Pilot_Dia_4=25 mm  [stored 0.082021 ft]; Pilot_Dia_5=17 mm; Pilot_top_1=688 mm; Pilot_top_ref=93 mm; Profile1_Height=496 mm; Profile1_Length=86 mm; Profile1_Length_2=58 mm; Profile_Dia=20 mm  [stored 0.0656168 ft]; Profile_Dia_2=20 mm  [stored 0.0656168 ft]; Profile_Dia_3=40 mm  [stored 0.131234 ft]; Profile_Dia_Ref=10 mm  [stored 0.0328084 ft]; Profile_Dia_Ref_2=40 mm  [stored 0.131234 ft]; Profile_height ref=50 mm  [stored 0.164042 ft]; T_Height=245 mm; T_Height_2=210 mm; T_Height_Ref_1=35 mm  [stored 0.114829 ft]; T_Height_Ref_2=41 mm; T_ref=656 mm; Top_Profile=554 mm; Top_Profile_Ref=559 mm; W=1010 mm; W_Ref=982 mm
- 879-0450-00-14400319999_DN450_PN16: Body_Collar_Dia=109 mm; Body_Collar_Dia_2=75 mm; Body_Flange_Dia=343 mm; Body_Flange_Dia_2=375 mm; Body_Height_1=300 mm; Body_Height_2=150 mm; Body_Height_3=120 mm; Body_Height_4=165 mm; Body_Top_Dia=44 mm; Body_Top_Dia_2=37 mm; Body_With_Dia=150 mm; Body_With_Dia_1=300 mm; Body_With_Dia_2=300 mm; Bolt_support=923 mm; Bolt_support_2=462 mm; Bolt_support_Dia=40 mm  [stored 0.131234 ft]; Bolt_support_lenght=245 mm; Bolt_support_lenght_2=255 mm; Bottom_profile=113 mm; D1=274 mm; D3=320 mm; DN=451 mm; Fillet_Length=20 mm  [stored 0.0656168 ft]; Fillet_Length_Ref=60 mm; Flange_thickness=30 mm  [stored 0.0984252 ft]; H=1130 mm; H3_Ref=1110 mm; ID=225 mm; L=1200 mm; L_Ref=570 mm; NV_Dia=200 mm; PG_Dia=150 mm; PG_Ref=200 mm; PG_depth=28 mm  [stored 0.0918635 ft]; PG_height=751 mm; PG_height_1=676 mm; PG_ref=235 mm; PR_1=55 mm; P_lenght=174 mm; Pilot_Dia_1=79 mm; Pilot_Dia_2=158 mm; Pilot_Dia_3=53 mm; Pilot_Dia_4=26 mm; Pilot_Dia_5=18 mm; Pilot_top_1=688 mm; Pilot_top_ref=93 mm; Profile1_Height=495 mm; Profile1_Length=86 mm; Profile1_Length_2=58 mm; Profile_Dia=20 mm  [stored 0.0656168 ft]; Profile_Dia_2=20 mm  [stored 0.0656168 ft]; Profile_Dia_3=40 mm  [stored 0.131234 ft]; Profile_Dia_Ref=10 mm  [stored 0.0328084 ft]; Profile_Dia_Ref_2=40 mm  [stored 0.131234 ft]; Profile_height ref=50 mm  [stored 0.164042 ft]; T_Height=245 mm; T_Height_2=210 mm; T_Height_Ref_1=35 mm  [stored 0.114829 ft]; T_Height_Ref_2=41 mm; T_ref=656 mm; Top_Profile=554 mm; Top_Profile_Ref=559 mm; W=1010 mm; W_Ref=982 mm
- 879-0450-00-144003199A0_DN450_PN16: Body_Collar_Dia=109 mm; Body_Collar_Dia_2=75 mm; Body_Flange_Dia=343 mm; Body_Flange_Dia_2=375 mm; Body_Height_1=300 mm; Body_Height_2=150 mm; Body_Height_3=120 mm; Body_Height_4=165 mm; Body_Top_Dia=44 mm; Body_Top_Dia_2=37 mm; Body_With_Dia=150 mm; Body_With_Dia_1=300 mm; Body_With_Dia_2=300 mm; Bolt_support=923 mm; Bolt_support_2=462 mm; Bolt_support_Dia=40 mm  [stored 0.131234 ft]; Bolt_support_lenght=245 mm; Bolt_support_lenght_2=255 mm; Bottom_profile=113 mm; D1=274 mm; D3=320 mm; DN=451 mm; Fillet_Length=20 mm  [stored 0.0656168 ft]; Fillet_Length_Ref=60 mm; Flange_thickness=30 mm  [stored 0.0984252 ft]; H=1220 mm; H3_Ref=1200 mm; ID=225 mm; L=1200 mm; L_Ref=570 mm; NV_Dia=200 mm; PG_Dia=150 mm; PG_Ref=200 mm; PG_depth=28 mm  [stored 0.0918635 ft]; PG_height=771 mm; PG_height_1=696 mm; PG_ref=235 mm; PR_1=76 mm; P_lenght=174 mm; Pilot_Dia_1=79 mm; Pilot_Dia_2=158 mm; Pilot_Dia_3=53 mm; Pilot_Dia_4=26 mm; Pilot_Dia_5=18 mm; Pilot_top_1=733 mm; Pilot_top_ref=138 mm; Profile1_Height=496 mm; Profile1_Length=86 mm; Profile1_Length_2=58 mm; Profile_Dia=20 mm  [stored 0.0656168 ft]; Profile_Dia_2=20 mm  [stored 0.0656168 ft]; Profile_Dia_3=40 mm  [stored 0.131234 ft]; Profile_Dia_Ref=10 mm  [stored 0.0328084 ft]; Profile_Dia_Ref_2=40 mm  [stored 0.131234 ft]; Profile_height ref=50 mm  [stored 0.164042 ft]; T_Height=335 mm; T_Height_2=287 mm; T_Height_Ref_1=48 mm; T_Height_Ref_2=56 mm; T_ref=697 mm; Top_Profile=554 mm; Top_Profile_Ref=559 mm; W=1010 mm; W_Ref=982 mm
- 879-0450-00-14400329999_DN450_PN16: Body_Collar_Dia=109 mm; Body_Collar_Dia_2=75 mm; Body_Flange_Dia=343 mm; Body_Flange_Dia_2=375 mm; Body_Height_1=300 mm; Body_Height_2=150 mm; Body_Height_3=120 mm; Body_Height_4=165 mm; Body_Top_Dia=44 mm; Body_Top_Dia_2=37 mm; Body_With_Dia=150 mm; Body_With_Dia_1=300 mm; Body_With_Dia_2=300 mm; Bolt_support=923 mm; Bolt_support_2=462 mm; Bolt_support_Dia=40 mm  [stored 0.131234 ft]; Bolt_support_lenght=245 mm; Bolt_support_lenght_2=255 mm; Bottom_profile=113 mm; D1=274 mm; D3=320 mm; DN=451 mm; Fillet_Length=20 mm  [stored 0.0656168 ft]; Fillet_Length_Ref=60 mm; Flange_thickness=30 mm  [stored 0.0984252 ft]; H=1130 mm; H3_Ref=1110 mm; ID=225 mm; L=1200 mm; L_Ref=570 mm; NV_Dia=200 mm; PG_Dia=150 mm; PG_Ref=200 mm; PG_depth=28 mm  [stored 0.0918635 ft]; PG_height=734 mm; PG_height_1=659 mm; PG_ref=235 mm; PR_1=60 mm; P_lenght=166 mm; Pilot_Dia_1=76 mm; Pilot_Dia_2=151 mm; Pilot_Dia_3=50 mm  [stored 0.164042 ft]; Pilot_Dia_4=25 mm  [stored 0.082021 ft]; Pilot_Dia_5=17 mm; Pilot_top_1=688 mm; Pilot_top_ref=93 mm; Profile1_Height=474 mm; Profile1_Length=86 mm; Profile1_Length_2=58 mm; Profile_Dia=20 mm  [stored 0.0656168 ft]; Profile_Dia_2=20 mm  [stored 0.0656168 ft]; Profile_Dia_3=40 mm  [stored 0.131234 ft]; Profile_Dia_Ref=10 mm  [stored 0.0328084 ft]; Profile_Dia_Ref_2=40 mm  [stored 0.131234 ft]; Profile_height ref=50 mm  [stored 0.164042 ft]; T_Height=266 mm; T_Height_2=228 mm; T_Height_Ref_1=38 mm  [stored 0.124672 ft]; T_Height_Ref_2=44 mm; T_ref=644 mm; Top_Profile=554 mm; Top_Profile_Ref=559 mm; W=1010 mm; W_Ref=982 mm
- 879-0450-00-14400339999_DN450_PN16: Body_Collar_Dia=109 mm; Body_Collar_Dia_2=75 mm; Body_Flange_Dia=343 mm; Body_Flange_Dia_2=375 mm; Body_Height_1=300 mm; Body_Height_2=150 mm; Body_Height_3=120 mm; Body_Height_4=165 mm; Body_Top_Dia=44 mm; Body_Top_Dia_2=37 mm; Body_With_Dia=150 mm; Body_With_Dia_1=300 mm; Body_With_Dia_2=300 mm; Bolt_support=923 mm; Bolt_support_2=462 mm; Bolt_support_Dia=40 mm  [stored 0.131234 ft]; Bolt_support_lenght=245 mm; Bolt_support_lenght_2=255 mm; Bottom_profile=113 mm; D1=274 mm; D3=320 mm; DN=451 mm; Fillet_Length=20 mm  [stored 0.0656168 ft]; Fillet_Length_Ref=60 mm; Flange_thickness=30 mm  [stored 0.0984252 ft]; H=1130 mm; H3_Ref=1110 mm; ID=225 mm; L=1200 mm; L_Ref=570 mm; NV_Dia=200 mm; PG_Dia=150 mm; PG_Ref=200 mm; PG_depth=28 mm  [stored 0.0918635 ft]; PG_height=751 mm; PG_height_1=676 mm; PG_ref=235 mm; PR_1=55 mm; P_lenght=166 mm; Pilot_Dia_1=76 mm; Pilot_Dia_2=151 mm; Pilot_Dia_3=50 mm  [stored 0.164042 ft]; Pilot_Dia_4=25 mm  [stored 0.082021 ft]; Pilot_Dia_5=17 mm; Pilot_top_1=688 mm; Pilot_top_ref=93 mm; Profile1_Height=496 mm; Profile1_Length=86 mm; Profile1_Length_2=58 mm; Profile_Dia=20 mm  [stored 0.0656168 ft]; Profile_Dia_2=20 mm  [stored 0.0656168 ft]; Profile_Dia_3=40 mm  [stored 0.131234 ft]; Profile_Dia_Ref=10 mm  [stored 0.0328084 ft]; Profile_Dia_Ref_2=40 mm  [stored 0.131234 ft]; Profile_height ref=50 mm  [stored 0.164042 ft]; T_Height=245 mm; T_Height_2=210 mm; T_Height_Ref_1=35 mm  [stored 0.114829 ft]; T_Height_Ref_2=41 mm; T_ref=656 mm; Top_Profile=554 mm; Top_Profile_Ref=559 mm; W=1010 mm; W_Ref=982 mm
- 879-0500-00-04400309999_DN500_PN10: Body_Collar_Dia=114 mm; Body_Collar_Dia_2=78 mm; Body_Flange_Dia=357 mm; Body_Flange_Dia_2=391 mm; Body_Height_1=313 mm; Body_Height_2=156 mm; Body_Height_3=125 mm; Body_Height_4=171 mm; Body_Top_Dia=46 mm  [stored 0.150919 ft]; Body_Top_Dia_2=39 mm  [stored 0.127953 ft]; Body_With_Dia=156 mm; Body_With_Dia_1=313 mm; Body_With_Dia_2=313 mm; Bolt_support=962 mm; Bolt_support_2=481 mm; Bolt_support_Dia=50 mm  [stored 0.164042 ft]; Bolt_support_lenght=270 mm; Bolt_support_lenght_2=280 mm; Bottom_profile=125 mm; D1=291 mm; D3=335 mm; DN=500 mm; Fillet_Length=25 mm  [stored 0.082021 ft]; Fillet_Length_Ref=75 mm; Flange_thickness=32 mm; H=1315 mm; H3_Ref=1290 mm; ID=250 mm; L=1250 mm; L_Ref=594 mm; NV_Dia=220 mm; PG_Dia=167 mm; PG_Ref=208 mm; PG_depth=35 mm  [stored 0.114829 ft]; PG_height=821 mm; PG_height_1=737 mm; PG_ref=260 mm; PR_1=88 mm; P_lenght=183 mm; Pilot_Dia_1=83 mm; Pilot_Dia_2=166 mm; Pilot_Dia_3=55 mm; Pilot_Dia_4=28 mm  [stored 0.0918635 ft]; Pilot_Dia_5=18 mm; Pilot_top_1=782 mm; Pilot_top_ref=163 mm; Profile1_Height=506 mm; Profile1_Length=91 mm; Profile1_Length_2=60 mm; Profile_Dia=25 mm  [stored 0.082021 ft]; Profile_Dia_2=25 mm  [stored 0.082021 ft]; Profile_Dia_3=50 mm  [stored 0.164042 ft]; Profile_Dia_Ref=13 mm; Profile_Dia_Ref_2=50 mm  [stored 0.164042 ft]; Profile_height ref=60 mm; T_Height=389 mm; T_Height_2=333 mm; T_Height_Ref_1=56 mm; T_Height_Ref_2=65 mm; T_ref=742 mm; Top_Profile=577 mm; Top_Profile_Ref=582 mm; W=1085 mm; W_Ref=1050 mm
- 879-0500-00-04400319999_DN500_PN10: Body_Collar_Dia=114 mm; Body_Collar_Dia_2=78 mm; Body_Flange_Dia=357 mm; Body_Flange_Dia_2=391 mm; Body_Height_1=313 mm; Body_Height_2=156 mm; Body_Height_3=125 mm; Body_Height_4=171 mm; Body_Top_Dia=46 mm  [stored 0.150919 ft]; Body_Top_Dia_2=39 mm  [stored 0.127953 ft]; Body_With_Dia=156 mm; Body_With_Dia_1=313 mm; Body_With_Dia_2=313 mm; Bolt_support=962 mm; Bolt_support_2=481 mm; Bolt_support_Dia=50 mm  [stored 0.164042 ft]; Bolt_support_lenght=270 mm; Bolt_support_lenght_2=280 mm; Bottom_profile=125 mm; D1=291 mm; D3=335 mm; DN=500 mm; Fillet_Length=25 mm  [stored 0.082021 ft]; Fillet_Length_Ref=75 mm; Flange_thickness=32 mm; H=1315 mm; H3_Ref=1290 mm; ID=250 mm; L=1250 mm; L_Ref=594 mm; NV_Dia=220 mm; PG_Dia=167 mm; PG_Ref=208 mm; PG_depth=35 mm  [stored 0.114829 ft]; PG_height=821 mm; PG_height_1=737 mm; PG_ref=260 mm; PR_1=88 mm; P_lenght=183 mm; Pilot_Dia_1=83 mm; Pilot_Dia_2=166 mm; Pilot_Dia_3=55 mm; Pilot_Dia_4=28 mm  [stored 0.0918635 ft]; Pilot_Dia_5=18 mm; Pilot_top_1=782 mm; Pilot_top_ref=163 mm; Profile1_Height=506 mm; Profile1_Length=91 mm; Profile1_Length_2=60 mm; Profile_Dia=25 mm  [stored 0.082021 ft]; Profile_Dia_2=25 mm  [stored 0.082021 ft]; Profile_Dia_3=50 mm  [stored 0.164042 ft]; Profile_Dia_Ref=13 mm; Profile_Dia_Ref_2=50 mm  [stored 0.164042 ft]; Profile_height ref=60 mm; T_Height=389 mm; T_Height_2=333 mm; T_Height_Ref_1=56 mm; T_Height_Ref_2=65 mm; T_ref=742 mm; Top_Profile=577 mm; Top_Profile_Ref=582 mm; W=1085 mm; W_Ref=1050 mm
- 879-0500-00-044003199A0_DN500_PN10: Body_Collar_Dia=114 mm; Body_Collar_Dia_2=78 mm; Body_Flange_Dia=357 mm; Body_Flange_Dia_2=391 mm; Body_Height_1=313 mm; Body_Height_2=156 mm; Body_Height_3=125 mm; Body_Height_4=171 mm; Body_Top_Dia=46 mm  [stored 0.150919 ft]; Body_Top_Dia_2=39 mm  [stored 0.127953 ft]; Body_With_Dia=156 mm; Body_With_Dia_1=313 mm; Body_With_Dia_2=313 mm; Bolt_support=962 mm; Bolt_support_2=481 mm; Bolt_support_Dia=50 mm  [stored 0.164042 ft]; Bolt_support_lenght=270 mm; Bolt_support_lenght_2=280 mm; Bottom_profile=125 mm; D1=291 mm; D3=335 mm; DN=500 mm; Fillet_Length=25 mm  [stored 0.082021 ft]; Fillet_Length_Ref=75 mm; Flange_thickness=32 mm; H=1408 mm; H3_Ref=1383 mm; ID=250 mm; L=1250 mm; L_Ref=594 mm; NV_Dia=220 mm; PG_Dia=167 mm; PG_Ref=208 mm; PG_depth=35 mm  [stored 0.114829 ft]; PG_height=842 mm; PG_height_1=758 mm; PG_ref=260 mm; PR_1=109 mm; P_lenght=196 mm; Pilot_Dia_1=89 mm; Pilot_Dia_2=178 mm; Pilot_Dia_3=59 mm; Pilot_Dia_4=30 mm  [stored 0.0984252 ft]; Pilot_Dia_5=20 mm  [stored 0.0656168 ft]; Pilot_top_1=828 mm; Pilot_top_ref=210 mm; Profile1_Height=506 mm; Profile1_Length=91 mm; Profile1_Length_2=60 mm; Profile_Dia=25 mm  [stored 0.082021 ft]; Profile_Dia_2=25 mm  [stored 0.082021 ft]; Profile_Dia_3=50 mm  [stored 0.164042 ft]; Profile_Dia_Ref=13 mm; Profile_Dia_Ref_2=50 mm  [stored 0.164042 ft]; Profile_height ref=60 mm; T_Height=482 mm; T_Height_2=413 mm; T_Height_Ref_1=69 mm; T_Height_Ref_2=80 mm; T_ref=784 mm; Top_Profile=577 mm; Top_Profile_Ref=582 mm; W=1085 mm; W_Ref=1050 mm
- 879-0500-00-04400339999_DN500_PN10: Body_Collar_Dia=114 mm; Body_Collar_Dia_2=78 mm; Body_Flange_Dia=357 mm; Body_Flange_Dia_2=391 mm; Body_Height_1=313 mm; Body_Height_2=156 mm; Body_Height_3=125 mm; Body_Height_4=171 mm; Body_Top_Dia=46 mm  [stored 0.150919 ft]; Body_Top_Dia_2=39 mm  [stored 0.127953 ft]; Body_With_Dia=156 mm; Body_With_Dia_1=313 mm; Body_With_Dia_2=313 mm; Bolt_support=962 mm; Bolt_support_2=481 mm; Bolt_support_Dia=50 mm  [stored 0.164042 ft]; Bolt_support_lenght=270 mm; Bolt_support_lenght_2=280 mm; Bottom_profile=125 mm; D1=291 mm; D3=335 mm; DN=500 mm; Fillet_Length=25 mm  [stored 0.082021 ft]; Fillet_Length_Ref=75 mm; Flange_thickness=32 mm; H=1315 mm; H3_Ref=1290 mm; ID=250 mm; L=1250 mm; L_Ref=594 mm; NV_Dia=220 mm; PG_Dia=167 mm; PG_Ref=208 mm; PG_depth=35 mm  [stored 0.114829 ft]; PG_height=838 mm; PG_height_1=754 mm; PG_ref=260 mm; PR_1=83 mm; P_lenght=196 mm; Pilot_Dia_1=89 mm; Pilot_Dia_2=178 mm; Pilot_Dia_3=59 mm; Pilot_Dia_4=30 mm  [stored 0.0984252 ft]; Pilot_Dia_5=20 mm  [stored 0.0656168 ft]; Pilot_top_1=782 mm; Pilot_top_ref=163 mm; Profile1_Height=528 mm; Profile1_Length=91 mm; Profile1_Length_2=60 mm; Profile_Dia=25 mm  [stored 0.082021 ft]; Profile_Dia_2=25 mm  [stored 0.082021 ft]; Profile_Dia_3=50 mm  [stored 0.164042 ft]; Profile_Dia_Ref=13 mm; Profile_Dia_Ref_2=50 mm  [stored 0.164042 ft]; Profile_height ref=60 mm; T_Height=367 mm; T_Height_2=315 mm; T_Height_Ref_1=52 mm; T_Height_Ref_2=61 mm; T_ref=754 mm; Top_Profile=577 mm; Top_Profile_Ref=582 mm; W=1085 mm; W_Ref=1050 mm
- 879-0500-00-14400309999_DN500_PN16: Body_Collar_Dia=114 mm; Body_Collar_Dia_2=78 mm; Body_Flange_Dia=357 mm; Body_Flange_Dia_2=391 mm; Body_Height_1=313 mm; Body_Height_2=156 mm; Body_Height_3=125 mm; Body_Height_4=171 mm; Body_Top_Dia=46 mm  [stored 0.150919 ft]; Body_Top_Dia_2=39 mm  [stored 0.127953 ft]; Body_With_Dia=156 mm; Body_With_Dia_1=313 mm; Body_With_Dia_2=313 mm; Bolt_support=962 mm; Bolt_support_2=481 mm; Bolt_support_Dia=50 mm  [stored 0.164042 ft]; Bolt_support_lenght=270 mm; Bolt_support_lenght_2=280 mm; Bottom_profile=125 mm; D1=291 mm; D3=335 mm; DN=500 mm; Fillet_Length=25 mm  [stored 0.082021 ft]; Fillet_Length_Ref=75 mm; Flange_thickness=32 mm; H=1315 mm; H3_Ref=1290 mm; ID=250 mm; L=1250 mm; L_Ref=594 mm; NV_Dia=220 mm; PG_Dia=167 mm; PG_Ref=208 mm; PG_depth=35 mm  [stored 0.114829 ft]; PG_height=821 mm; PG_height_1=737 mm; PG_ref=260 mm; PR_1=88 mm; P_lenght=183 mm; Pilot_Dia_1=83 mm; Pilot_Dia_2=166 mm; Pilot_Dia_3=55 mm; Pilot_Dia_4=28 mm  [stored 0.0918635 ft]; Pilot_Dia_5=18 mm; Pilot_top_1=782 mm; Pilot_top_ref=163 mm; Profile1_Height=506 mm; Profile1_Length=91 mm; Profile1_Length_2=60 mm; Profile_Dia=25 mm  [stored 0.082021 ft]; Profile_Dia_2=25 mm  [stored 0.082021 ft]; Profile_Dia_3=50 mm  [stored 0.164042 ft]; Profile_Dia_Ref=13 mm; Profile_Dia_Ref_2=50 mm  [stored 0.164042 ft]; Profile_height ref=60 mm; T_Height=389 mm; T_Height_2=333 mm; T_Height_Ref_1=56 mm; T_Height_Ref_2=65 mm; T_ref=742 mm; Top_Profile=577 mm; Top_Profile_Ref=582 mm; W=1085 mm; W_Ref=1050 mm
- 879-0500-00-14400319999_DN500_PN16: Body_Collar_Dia=114 mm; Body_Collar_Dia_2=78 mm; Body_Flange_Dia=357 mm; Body_Flange_Dia_2=391 mm; Body_Height_1=313 mm; Body_Height_2=156 mm; Body_Height_3=125 mm; Body_Height_4=171 mm; Body_Top_Dia=46 mm  [stored 0.150919 ft]; Body_Top_Dia_2=39 mm  [stored 0.127953 ft]; Body_With_Dia=156 mm; Body_With_Dia_1=313 mm; Body_With_Dia_2=313 mm; Bolt_support=962 mm; Bolt_support_2=481 mm; Bolt_support_Dia=50 mm  [stored 0.164042 ft]; Bolt_support_lenght=270 mm; Bolt_support_lenght_2=280 mm; Bottom_profile=125 mm; D1=305 mm; D3=358 mm; DN=501 mm; Fillet_Length=25 mm  [stored 0.082021 ft]; Fillet_Length_Ref=75 mm; Flange_thickness=32 mm; H=1315 mm; H3_Ref=1290 mm; ID=250 mm; L=1250 mm; L_Ref=594 mm; NV_Dia=220 mm; PG_Dia=167 mm; PG_Ref=208 mm; PG_depth=35 mm  [stored 0.114829 ft]; PG_height=816 mm; PG_height_1=732 mm; PG_ref=260 mm; PR_1=83 mm; P_lenght=196 mm; Pilot_Dia_1=89 mm; Pilot_Dia_2=178 mm; Pilot_Dia_3=59 mm; Pilot_Dia_4=30 mm  [stored 0.0984252 ft]; Pilot_Dia_5=20 mm  [stored 0.0656168 ft]; Pilot_top_1=771 mm; Pilot_top_ref=152 mm; Profile1_Height=506 mm; Profile1_Length=97 mm; Profile1_Length_2=64 mm; Profile_Dia=25 mm  [stored 0.082021 ft]; Profile_Dia_2=25 mm  [stored 0.082021 ft]; Profile_Dia_3=50 mm  [stored 0.164042 ft]; Profile_Dia_Ref=13 mm; Profile_Dia_Ref_2=50 mm  [stored 0.164042 ft]; Profile_height ref=60 mm; T_Height=367 mm; T_Height_2=314 mm; T_Height_Ref_1=52 mm; T_Height_Ref_2=61 mm; T_ref=732 mm; Top_Profile=577 mm; Top_Profile_Ref=582 mm; W=1085 mm; W_Ref=1050 mm
- 879-0500-00-144003199A0_DN500_PN16: Body_Collar_Dia=114 mm; Body_Collar_Dia_2=78 mm; Body_Flange_Dia=357 mm; Body_Flange_Dia_2=391 mm; Body_Height_1=313 mm; Body_Height_2=156 mm; Body_Height_3=125 mm; Body_Height_4=171 mm; Body_Top_Dia=46 mm  [stored 0.150919 ft]; Body_Top_Dia_2=39 mm  [stored 0.127953 ft]; Body_With_Dia=156 mm; Body_With_Dia_1=313 mm; Body_With_Dia_2=313 mm; Bolt_support=962 mm; Bolt_support_2=481 mm; Bolt_support_Dia=50 mm  [stored 0.164042 ft]; Bolt_support_lenght=270 mm; Bolt_support_lenght_2=280 mm; Bottom_profile=125 mm; D1=305 mm; D3=358 mm; DN=501 mm; Fillet_Length=25 mm  [stored 0.082021 ft]; Fillet_Length_Ref=75 mm; Flange_thickness=32 mm; H=1408 mm; H3_Ref=1383 mm; ID=250 mm; L=1250 mm; L_Ref=594 mm; NV_Dia=220 mm; PG_Dia=167 mm; PG_Ref=208 mm; PG_depth=35 mm  [stored 0.114829 ft]; PG_height=854 mm; PG_height_1=770 mm; PG_ref=260 mm; PR_1=99 mm; P_lenght=196 mm; Pilot_Dia_1=89 mm; Pilot_Dia_2=178 mm; Pilot_Dia_3=59 mm; Pilot_Dia_4=30 mm  [stored 0.0984252 ft]; Pilot_Dia_5=20 mm  [stored 0.0656168 ft]; Pilot_top_1=817 mm; Pilot_top_ref=198 mm; Profile1_Height=528 mm; Profile1_Length=97 mm; Profile1_Length_2=64 mm; Profile_Dia=25 mm  [stored 0.082021 ft]; Profile_Dia_2=25 mm  [stored 0.082021 ft]; Profile_Dia_3=50 mm  [stored 0.164042 ft]; Profile_Dia_Ref=13 mm; Profile_Dia_Ref_2=50 mm  [stored 0.164042 ft]; Profile_height ref=60 mm; T_Height=438 mm; T_Height_2=375 mm; T_Height_Ref_1=63 mm; T_Height_Ref_2=73 mm; T_ref=786 mm; Top_Profile=577 mm; Top_Profile_Ref=582 mm; W=1085 mm; W_Ref=1050 mm
- 879-0500-00-14400329999_DN500_PN16: Body_Collar_Dia=114 mm; Body_Collar_Dia_2=78 mm; Body_Flange_Dia=357 mm; Body_Flange_Dia_2=391 mm; Body_Height_1=313 mm; Body_Height_2=156 mm; Body_Height_3=125 mm; Body_Height_4=171 mm; Body_Top_Dia=46 mm  [stored 0.150919 ft]; Body_Top_Dia_2=39 mm  [stored 0.127953 ft]; Body_With_Dia=156 mm; Body_With_Dia_1=313 mm; Body_With_Dia_2=313 mm; Bolt_support=962 mm; Bolt_support_2=481 mm; Bolt_support_Dia=50 mm  [stored 0.164042 ft]; Bolt_support_lenght=270 mm; Bolt_support_lenght_2=280 mm; Bottom_profile=125 mm; D1=305 mm; D3=358 mm; DN=501 mm; Fillet_Length=25 mm  [stored 0.082021 ft]; Fillet_Length_Ref=75 mm; Flange_thickness=32 mm; H=1315 mm; H3_Ref=1290 mm; ID=250 mm; L=1250 mm; L_Ref=594 mm; NV_Dia=220 mm; PG_Dia=167 mm; PG_Ref=208 mm; PG_depth=35 mm  [stored 0.114829 ft]; PG_height=816 mm; PG_height_1=732 mm; PG_ref=260 mm; PR_1=83 mm; P_lenght=183 mm; Pilot_Dia_1=83 mm; Pilot_Dia_2=166 mm; Pilot_Dia_3=55 mm; Pilot_Dia_4=28 mm  [stored 0.0918635 ft]; Pilot_Dia_5=18 mm; Pilot_top_1=771 mm; Pilot_top_ref=152 mm; Profile1_Height=506 mm; Profile1_Length=97 mm; Profile1_Length_2=64 mm; Profile_Dia=25 mm  [stored 0.082021 ft]; Profile_Dia_2=25 mm  [stored 0.082021 ft]; Profile_Dia_3=50 mm  [stored 0.164042 ft]; Profile_Dia_Ref=13 mm; Profile_Dia_Ref_2=50 mm  [stored 0.164042 ft]; Profile_height ref=60 mm; T_Height=367 mm; T_Height_2=314 mm; T_Height_Ref_1=52 mm; T_Height_Ref_2=61 mm; T_ref=732 mm; Top_Profile=577 mm; Top_Profile_Ref=582 mm; W=1085 mm; W_Ref=1050 mm
- 879-0500-00-14400339999_DN500_PN16: Body_Collar_Dia=114 mm; Body_Collar_Dia_2=78 mm; Body_Flange_Dia=357 mm; Body_Flange_Dia_2=391 mm; Body_Height_1=313 mm; Body_Height_2=156 mm; Body_Height_3=125 mm; Body_Height_4=171 mm; Body_Top_Dia=46 mm  [stored 0.150919 ft]; Body_Top_Dia_2=39 mm  [stored 0.127953 ft]; Body_With_Dia=156 mm; Body_With_Dia_1=313 mm; Body_With_Dia_2=313 mm; Bolt_support=962 mm; Bolt_support_2=481 mm; Bolt_support_Dia=50 mm  [stored 0.164042 ft]; Bolt_support_lenght=270 mm; Bolt_support_lenght_2=280 mm; Bottom_profile=125 mm; D1=305 mm; D3=358 mm; DN=501 mm; Fillet_Length=25 mm  [stored 0.082021 ft]; Fillet_Length_Ref=75 mm; Flange_thickness=32 mm; H=1315 mm; H3_Ref=1290 mm; ID=250 mm; L=1250 mm; L_Ref=594 mm; NV_Dia=220 mm; PG_Dia=167 mm; PG_Ref=208 mm; PG_depth=35 mm  [stored 0.114829 ft]; PG_height=816 mm; PG_height_1=732 mm; PG_ref=260 mm; PR_1=83 mm; P_lenght=183 mm; Pilot_Dia_1=83 mm; Pilot_Dia_2=166 mm; Pilot_Dia_3=55 mm; Pilot_Dia_4=28 mm  [stored 0.0918635 ft]; Pilot_Dia_5=18 mm; Pilot_top_1=771 mm; Pilot_top_ref=152 mm; Profile1_Height=506 mm; Profile1_Length=97 mm; Profile1_Length_2=64 mm; Profile_Dia=25 mm  [stored 0.082021 ft]; Profile_Dia_2=25 mm  [stored 0.082021 ft]; Profile_Dia_3=50 mm  [stored 0.164042 ft]; Profile_Dia_Ref=13 mm; Profile_Dia_Ref_2=50 mm  [stored 0.164042 ft]; Profile_height ref=60 mm; T_Height=367 mm; T_Height_2=314 mm; T_Height_Ref_1=52 mm; T_Height_Ref_2=61 mm; T_ref=732 mm; Top_Profile=577 mm; Top_Profile_Ref=582 mm; W=1085 mm; W_Ref=1050 mm
- 879-0600-00-04400309999_DN600_PN10: Body_Collar_Dia=132 mm; Body_Collar_Dia_2=91 mm; Body_Flange_Dia=414 mm; Body_Flange_Dia_2=453 mm; Body_Height_1=363 mm; Body_Height_2=181 mm; Body_Height_3=145 mm; Body_Height_4=196 mm; Body_Top_Dia=54 mm; Body_Top_Dia_2=45 mm  [stored 0.147638 ft]; Body_With_Dia=181 mm; Body_With_Dia_1=363 mm; Body_With_Dia_2=363 mm; Bolt_support=1115 mm; Bolt_support_2=558 mm; Bolt_support_Dia=60 mm; Bolt_support_lenght=320 mm; Bolt_support_lenght_2=330 mm; Bottom_profile=150 mm; D1=341 mm; D3=390 mm; DN=600 mm; Fillet_Length=30 mm  [stored 0.0984252 ft]; Fillet_Length_Ref=90 mm; Flange_thickness=36 mm  [stored 0.11811 ft]; H=1425 mm; H3_Ref=1395 mm; ID=300 mm; L=1450 mm; L_Ref=689 mm; NV_Dia=230 mm; PG_Dia=200 mm; PG_Ref=242 mm; PG_depth=42 mm  [stored 0.137795 ft]; PG_height=931 mm; PG_height_1=831 mm; PG_ref=310 mm; PR_1=80 mm; P_lenght=216 mm; Pilot_Dia_1=98 mm; Pilot_Dia_2=196 mm; Pilot_Dia_3=65 mm; Pilot_Dia_4=33 mm; Pilot_Dia_5=22 mm  [stored 0.0721785 ft]; Pilot_top_1=854 mm; Pilot_top_ref=141 mm; Profile1_Height=581 mm; Profile1_Length=105 mm; Profile1_Length_2=70 mm; Profile_Dia=30 mm  [stored 0.0984252 ft]; Profile_Dia_2=30 mm  [stored 0.0984252 ft]; Profile_Dia_3=60 mm; Profile_Dia_Ref=15 mm  [stored 0.0492126 ft]; Profile_Dia_Ref_2=60 mm; Profile_height ref=70 mm; T_Height=354 mm; T_Height_2=303 mm; T_Height_Ref_1=51 mm; T_Height_Ref_2=59 mm; T_ref=811 mm; Top_Profile=669 mm; Top_Profile_Ref=674 mm; W=1210 mm; W_Ref=1168 mm
- 879-0600-00-04400319999_DN600_PN10: Body_Collar_Dia=132 mm; Body_Collar_Dia_2=91 mm; Body_Flange_Dia=414 mm; Body_Flange_Dia_2=453 mm; Body_Height_1=363 mm; Body_Height_2=181 mm; Body_Height_3=145 mm; Body_Height_4=196 mm; Body_Top_Dia=54 mm; Body_Top_Dia_2=45 mm  [stored 0.147638 ft]; Body_With_Dia=181 mm; Body_With_Dia_1=363 mm; Body_With_Dia_2=363 mm; Bolt_support=1115 mm; Bolt_support_2=558 mm; Bolt_support_Dia=60 mm; Bolt_support_lenght=320 mm; Bolt_support_lenght_2=330 mm; Bottom_profile=150 mm; D1=341 mm; D3=390 mm; DN=600 mm; Fillet_Length=30 mm  [stored 0.0984252 ft]; Fillet_Length_Ref=90 mm; Flange_thickness=36 mm  [stored 0.11811 ft]; H=1425 mm; H3_Ref=1395 mm; ID=300 mm; L=1450 mm; L_Ref=689 mm; NV_Dia=230 mm; PG_Dia=200 mm; PG_Ref=242 mm; PG_depth=42 mm  [stored 0.137795 ft]; PG_height=965 mm; PG_height_1=865 mm; PG_ref=310 mm; PR_1=70 mm; P_lenght=216 mm; Pilot_Dia_1=98 mm; Pilot_Dia_2=196 mm; Pilot_Dia_3=65 mm; Pilot_Dia_4=33 mm; Pilot_Dia_5=22 mm  [stored 0.0721785 ft]; Pilot_top_1=854 mm; Pilot_top_ref=141 mm; Profile1_Height=625 mm; Profile1_Length=105 mm; Profile1_Length_2=70 mm; Profile_Dia=30 mm  [stored 0.0984252 ft]; Profile_Dia_2=30 mm  [stored 0.0984252 ft]; Profile_Dia_3=60 mm; Profile_Dia_Ref=15 mm  [stored 0.0492126 ft]; Profile_Dia_Ref_2=60 mm; Profile_height ref=70 mm; T_Height=310 mm; T_Height_2=266 mm; T_Height_Ref_1=44 mm; T_Height_Ref_2=52 mm; T_ref=835 mm; Top_Profile=669 mm; Top_Profile_Ref=674 mm; W=1210 mm; W_Ref=1168 mm
- 879-0600-00-044003199A0_DN600_PN10: Body_Collar_Dia=132 mm; Body_Collar_Dia_2=91 mm; Body_Flange_Dia=414 mm; Body_Flange_Dia_2=453 mm; Body_Height_1=363 mm; Body_Height_2=181 mm; Body_Height_3=145 mm; Body_Height_4=196 mm; Body_Top_Dia=54 mm; Body_Top_Dia_2=45 mm  [stored 0.147638 ft]; Body_With_Dia=181 mm; Body_With_Dia_1=363 mm; Body_With_Dia_2=363 mm; Bolt_support=1115 mm; Bolt_support_2=558 mm; Bolt_support_Dia=60 mm; Bolt_support_lenght=320 mm; Bolt_support_lenght_2=330 mm; Bottom_profile=150 mm; D1=341 mm; D3=390 mm; DN=600 mm; Fillet_Length=30 mm  [stored 0.0984252 ft]; Fillet_Length_Ref=90 mm; Flange_thickness=36 mm  [stored 0.11811 ft]; H=1518 mm; H3_Ref=1488 mm; ID=300 mm; L=1450 mm; L_Ref=689 mm; NV_Dia=230 mm; PG_Dia=200 mm; PG_Ref=242 mm; PG_depth=42 mm  [stored 0.137795 ft]; PG_height=952 mm; PG_height_1=852 mm; PG_ref=310 mm; PR_1=101 mm; P_lenght=233 mm; Pilot_Dia_1=106 mm; Pilot_Dia_2=212 mm; Pilot_Dia_3=71 mm; Pilot_Dia_4=35 mm  [stored 0.114829 ft]; Pilot_Dia_5=24 mm  [stored 0.0787402 ft]; Pilot_top_1=901 mm; Pilot_top_ref=187 mm; Profile1_Height=581 mm; Profile1_Length=105 mm; Profile1_Length_2=70 mm; Profile_Dia=30 mm  [stored 0.0984252 ft]; Profile_Dia_2=30 mm  [stored 0.0984252 ft]; Profile_Dia_3=60 mm; Profile_Dia_Ref=15 mm  [stored 0.0492126 ft]; Profile_Dia_Ref_2=60 mm; Profile_height ref=70 mm; T_Height=447 mm; T_Height_2=383 mm; T_Height_Ref_1=64 mm; T_Height_Ref_2=75 mm; T_ref=853 mm; Top_Profile=669 mm; Top_Profile_Ref=674 mm; W=1210 mm; W_Ref=1168 mm
- 879-0600-00-04400329999_DN600_PN10: Body_Collar_Dia=132 mm; Body_Collar_Dia_2=91 mm; Body_Flange_Dia=414 mm; Body_Flange_Dia_2=453 mm; Body_Height_1=363 mm; Body_Height_2=181 mm; Body_Height_3=145 mm; Body_Height_4=196 mm; Body_Top_Dia=54 mm; Body_Top_Dia_2=45 mm  [stored 0.147638 ft]; Body_With_Dia=181 mm; Body_With_Dia_1=363 mm; Body_With_Dia_2=363 mm; Bolt_support=1115 mm; Bolt_support_2=558 mm; Bolt_support_Dia=60 mm; Bolt_support_lenght=320 mm; Bolt_support_lenght_2=330 mm; Bottom_profile=150 mm; D1=341 mm; D3=390 mm; DN=600 mm; Fillet_Length=30 mm  [stored 0.0984252 ft]; Fillet_Length_Ref=90 mm; Flange_thickness=36 mm  [stored 0.11811 ft]; H=1425 mm; H3_Ref=1395 mm; ID=300 mm; L=1450 mm; L_Ref=689 mm; NV_Dia=230 mm; PG_Dia=200 mm; PG_Ref=242 mm; PG_depth=42 mm  [stored 0.137795 ft]; PG_height=965 mm; PG_height_1=865 mm; PG_ref=310 mm; PR_1=70 mm; P_lenght=233 mm; Pilot_Dia_1=106 mm; Pilot_Dia_2=212 mm; Pilot_Dia_3=71 mm; Pilot_Dia_4=35 mm  [stored 0.114829 ft]; Pilot_Dia_5=24 mm  [stored 0.0787402 ft]; Pilot_top_1=854 mm; Pilot_top_ref=141 mm; Profile1_Height=625 mm; Profile1_Length=105 mm; Profile1_Length_2=70 mm; Profile_Dia=30 mm  [stored 0.0984252 ft]; Profile_Dia_2=30 mm  [stored 0.0984252 ft]; Profile_Dia_3=60 mm; Profile_Dia_Ref=15 mm  [stored 0.0492126 ft]; Profile_Dia_Ref_2=60 mm; Profile_height ref=70 mm; T_Height=310 mm; T_Height_2=266 mm; T_Height_Ref_1=44 mm; T_Height_Ref_2=52 mm; T_ref=835 mm; Top_Profile=669 mm; Top_Profile_Ref=674 mm; W=1210 mm; W_Ref=1168 mm
- 879-0600-00-04400339999_DN600_PN10: Body_Collar_Dia=132 mm; Body_Collar_Dia_2=91 mm; Body_Flange_Dia=414 mm; Body_Flange_Dia_2=453 mm; Body_Height_1=363 mm; Body_Height_2=181 mm; Body_Height_3=145 mm; Body_Height_4=196 mm; Body_Top_Dia=54 mm; Body_Top_Dia_2=45 mm  [stored 0.147638 ft]; Body_With_Dia=181 mm; Body_With_Dia_1=363 mm; Body_With_Dia_2=363 mm; Bolt_support=1115 mm; Bolt_support_2=558 mm; Bolt_support_Dia=60 mm; Bolt_support_lenght=320 mm; Bolt_support_lenght_2=330 mm; Bottom_profile=150 mm; D1=341 mm; D3=390 mm; DN=600 mm; Fillet_Length=30 mm  [stored 0.0984252 ft]; Fillet_Length_Ref=90 mm; Flange_thickness=36 mm  [stored 0.11811 ft]; H=1425 mm; H3_Ref=1395 mm; ID=300 mm; L=1450 mm; L_Ref=689 mm; NV_Dia=230 mm; PG_Dia=200 mm; PG_Ref=242 mm; PG_depth=42 mm  [stored 0.137795 ft]; PG_height=931 mm; PG_height_1=831 mm; PG_ref=310 mm; PR_1=80 mm; P_lenght=216 mm; Pilot_Dia_1=98 mm; Pilot_Dia_2=196 mm; Pilot_Dia_3=65 mm; Pilot_Dia_4=33 mm; Pilot_Dia_5=22 mm  [stored 0.0721785 ft]; Pilot_top_1=854 mm; Pilot_top_ref=141 mm; Profile1_Height=581 mm; Profile1_Length=105 mm; Profile1_Length_2=70 mm; Profile_Dia=30 mm  [stored 0.0984252 ft]; Profile_Dia_2=30 mm  [stored 0.0984252 ft]; Profile_Dia_3=60 mm; Profile_Dia_Ref=15 mm  [stored 0.0492126 ft]; Profile_Dia_Ref_2=60 mm; Profile_height ref=70 mm; T_Height=354 mm; T_Height_2=303 mm; T_Height_Ref_1=51 mm; T_Height_Ref_2=59 mm; T_ref=811 mm; Top_Profile=669 mm; Top_Profile_Ref=674 mm; W=1210 mm; W_Ref=1168 mm
- 879-0600-00-14400309999_DN600_PN16: Body_Collar_Dia=132 mm; Body_Collar_Dia_2=91 mm; Body_Flange_Dia=414 mm; Body_Flange_Dia_2=453 mm; Body_Height_1=363 mm; Body_Height_2=181 mm; Body_Height_3=145 mm; Body_Height_4=196 mm; Body_Top_Dia=54 mm; Body_Top_Dia_2=45 mm  [stored 0.147638 ft]; Body_With_Dia=181 mm; Body_With_Dia_1=363 mm; Body_With_Dia_2=363 mm; Bolt_support=1115 mm; Bolt_support_2=558 mm; Bolt_support_Dia=60 mm; Bolt_support_lenght=320 mm; Bolt_support_lenght_2=330 mm; Bottom_profile=150 mm; D1=360 mm; D3=420 mm; DN=601 mm; Fillet_Length=30 mm  [stored 0.0984252 ft]; Fillet_Length_Ref=90 mm; Flange_thickness=36 mm  [stored 0.11811 ft]; H=1425 mm; H3_Ref=1395 mm; ID=300 mm; L=1450 mm; L_Ref=689 mm; NV_Dia=230 mm; PG_Dia=200 mm; PG_Ref=242 mm; PG_depth=42 mm  [stored 0.137795 ft]; PG_height=959 mm; PG_height_1=858 mm; PG_ref=310 mm; PR_1=63 mm; P_lenght=216 mm; Pilot_Dia_1=98 mm; Pilot_Dia_2=196 mm; Pilot_Dia_3=65 mm; Pilot_Dia_4=33 mm; Pilot_Dia_5=22 mm  [stored 0.0721785 ft]; Pilot_top_1=839 mm; Pilot_top_ref=126 mm; Profile1_Height=625 mm; Profile1_Length=114 mm; Profile1_Length_2=76 mm; Profile_Dia=30 mm  [stored 0.0984252 ft]; Profile_Dia_2=30 mm  [stored 0.0984252 ft]; Profile_Dia_3=60 mm; Profile_Dia_Ref=15 mm  [stored 0.0492126 ft]; Profile_Dia_Ref_2=60 mm; Profile_height ref=70 mm; T_Height=280 mm; T_Height_2=240 mm; T_Height_Ref_1=40 mm  [stored 0.131234 ft]; T_Height_Ref_2=47 mm; T_ref=822 mm; Top_Profile=669 mm; Top_Profile_Ref=674 mm; W=1210 mm; W_Ref=1168 mm
- 879-0600-00-14400319999_DN600_PN16: Body_Collar_Dia=132 mm; Body_Collar_Dia_2=91 mm; Body_Flange_Dia=414 mm; Body_Flange_Dia_2=453 mm; Body_Height_1=363 mm; Body_Height_2=181 mm; Body_Height_3=145 mm; Body_Height_4=196 mm; Body_Top_Dia=54 mm; Body_Top_Dia_2=45 mm  [stored 0.147638 ft]; Body_With_Dia=181 mm; Body_With_Dia_1=363 mm; Body_With_Dia_2=363 mm; Bolt_support=1115 mm; Bolt_support_2=558 mm; Bolt_support_Dia=60 mm; Bolt_support_lenght=320 mm; Bolt_support_lenght_2=330 mm; Bottom_profile=150 mm; D1=360 mm; D3=420 mm; DN=601 mm; Fillet_Length=30 mm  [stored 0.0984252 ft]; Fillet_Length_Ref=90 mm; Flange_thickness=36 mm  [stored 0.11811 ft]; H=1425 mm; H3_Ref=1395 mm; ID=300 mm; L=1450 mm; L_Ref=689 mm; NV_Dia=230 mm; PG_Dia=200 mm; PG_Ref=242 mm; PG_depth=42 mm  [stored 0.137795 ft]; PG_height=924 mm; PG_height_1=824 mm; PG_ref=310 mm; PR_1=73 mm; P_lenght=233 mm; Pilot_Dia_1=106 mm; Pilot_Dia_2=212 mm; Pilot_Dia_3=71 mm; Pilot_Dia_4=35 mm  [stored 0.114829 ft]; Pilot_Dia_5=24 mm  [stored 0.0787402 ft]; Pilot_top_1=839 mm; Pilot_top_ref=126 mm; Profile1_Height=581 mm; Profile1_Length=114 mm; Profile1_Length_2=76 mm; Profile_Dia=30 mm  [stored 0.0984252 ft]; Profile_Dia_2=30 mm  [stored 0.0984252 ft]; Profile_Dia_3=60 mm; Profile_Dia_Ref=15 mm  [stored 0.0492126 ft]; Profile_Dia_Ref_2=60 mm; Profile_height ref=70 mm; T_Height=324 mm; T_Height_2=278 mm; T_Height_Ref_1=46 mm  [stored 0.150919 ft]; T_Height_Ref_2=54 mm; T_ref=798 mm; Top_Profile=669 mm; Top_Profile_Ref=674 mm; W=1210 mm; W_Ref=1168 mm
- 879-0600-00-144003199A0_DN600_PN16: Body_Collar_Dia=132 mm; Body_Collar_Dia_2=91 mm; Body_Flange_Dia=414 mm; Body_Flange_Dia_2=453 mm; Body_Height_1=363 mm; Body_Height_2=181 mm; Body_Height_3=145 mm; Body_Height_4=196 mm; Body_Top_Dia=54 mm; Body_Top_Dia_2=45 mm  [stored 0.147638 ft]; Body_With_Dia=181 mm; Body_With_Dia_1=363 mm; Body_With_Dia_2=363 mm; Bolt_support=1115 mm; Bolt_support_2=558 mm; Bolt_support_Dia=60 mm; Bolt_support_lenght=320 mm; Bolt_support_lenght_2=330 mm; Bottom_profile=150 mm; D1=360 mm; D3=420 mm; DN=601 mm; Fillet_Length=30 mm  [stored 0.0984252 ft]; Fillet_Length_Ref=90 mm; Flange_thickness=36 mm  [stored 0.11811 ft]; H=1518 mm; H3_Ref=1488 mm; ID=300 mm; L=1450 mm; L_Ref=689 mm; NV_Dia=230 mm; PG_Dia=200 mm; PG_Ref=242 mm; PG_depth=42 mm  [stored 0.137795 ft]; PG_height=980 mm; PG_height_1=879 mm; PG_ref=310 mm; PR_1=84 mm; P_lenght=233 mm; Pilot_Dia_1=106 mm; Pilot_Dia_2=212 mm; Pilot_Dia_3=71 mm; Pilot_Dia_4=35 mm  [stored 0.114829 ft]; Pilot_Dia_5=24 mm  [stored 0.0787402 ft]; Pilot_top_1=886 mm; Pilot_top_ref=172 mm; Profile1_Height=625 mm; Profile1_Length=114 mm; Profile1_Length_2=76 mm; Profile_Dia=30 mm  [stored 0.0984252 ft]; Profile_Dia_2=30 mm  [stored 0.0984252 ft]; Profile_Dia_3=60 mm; Profile_Dia_Ref=15 mm  [stored 0.0492126 ft]; Profile_Dia_Ref_2=60 mm; Profile_height ref=70 mm; T_Height=373 mm; T_Height_2=320 mm; T_Height_Ref_1=53 mm; T_Height_Ref_2=62 mm; T_ref=864 mm; Top_Profile=669 mm; Top_Profile_Ref=674 mm; W=1210 mm; W_Ref=1168 mm
- 879-0600-00-14400329999_DN600_PN16: Body_Collar_Dia=132 mm; Body_Collar_Dia_2=91 mm; Body_Flange_Dia=414 mm; Body_Flange_Dia_2=453 mm; Body_Height_1=363 mm; Body_Height_2=181 mm; Body_Height_3=145 mm; Body_Height_4=196 mm; Body_Top_Dia=54 mm; Body_Top_Dia_2=45 mm  [stored 0.147638 ft]; Body_With_Dia=181 mm; Body_With_Dia_1=363 mm; Body_With_Dia_2=363 mm; Bolt_support=1115 mm; Bolt_support_2=558 mm; Bolt_support_Dia=60 mm; Bolt_support_lenght=320 mm; Bolt_support_lenght_2=330 mm; Bottom_profile=150 mm; D1=360 mm; D3=420 mm; DN=601 mm; Fillet_Length=30 mm  [stored 0.0984252 ft]; Fillet_Length_Ref=90 mm; Flange_thickness=36 mm  [stored 0.11811 ft]; H=1425 mm; H3_Ref=1395 mm; ID=300 mm; L=1450 mm; L_Ref=689 mm; NV_Dia=230 mm; PG_Dia=200 mm; PG_Ref=242 mm; PG_depth=42 mm  [stored 0.137795 ft]; PG_height=925 mm; PG_height_1=824 mm; PG_ref=310 mm; PR_1=73 mm; P_lenght=216 mm; Pilot_Dia_1=98 mm; Pilot_Dia_2=196 mm; Pilot_Dia_3=65 mm; Pilot_Dia_4=33 mm; Pilot_Dia_5=22 mm  [stored 0.0721785 ft]; Pilot_top_1=839 mm; Pilot_top_ref=126 mm; Profile1_Height=581 mm; Profile1_Length=114 mm; Profile1_Length_2=76 mm; Profile_Dia=30 mm  [stored 0.0984252 ft]; Profile_Dia_2=30 mm  [stored 0.0984252 ft]; Profile_Dia_3=60 mm; Profile_Dia_Ref=15 mm  [stored 0.0492126 ft]; Profile_Dia_Ref_2=60 mm; Profile_height ref=70 mm; T_Height=324 mm; T_Height_2=278 mm; T_Height_Ref_1=46 mm  [stored 0.150919 ft]; T_Height_Ref_2=54 mm; T_ref=798 mm; Top_Profile=669 mm; Top_Profile_Ref=674 mm; W=1210 mm; W_Ref=1168 mm
- 879-0600-00-14400339999_DN600_PN16: Body_Collar_Dia=132 mm; Body_Collar_Dia_2=91 mm; Body_Flange_Dia=414 mm; Body_Flange_Dia_2=453 mm; Body_Height_1=363 mm; Body_Height_2=181 mm; Body_Height_3=145 mm; Body_Height_4=196 mm; Body_Top_Dia=54 mm; Body_Top_Dia_2=45 mm  [stored 0.147638 ft]; Body_With_Dia=181 mm; Body_With_Dia_1=363 mm; Body_With_Dia_2=363 mm; Bolt_support=1115 mm; Bolt_support_2=558 mm; Bolt_support_Dia=60 mm; Bolt_support_lenght=320 mm; Bolt_support_lenght_2=330 mm; Bottom_profile=150 mm; D1=360 mm; D3=420 mm; DN=601 mm; Fillet_Length=30 mm  [stored 0.0984252 ft]; Fillet_Length_Ref=90 mm; Flange_thickness=36 mm  [stored 0.11811 ft]; H=1425 mm; H3_Ref=1395 mm; ID=300 mm; L=1450 mm; L_Ref=689 mm; NV_Dia=230 mm; PG_Dia=200 mm; PG_Ref=242 mm; PG_depth=42 mm  [stored 0.137795 ft]; PG_height=959 mm; PG_height_1=858 mm; PG_ref=310 mm; PR_1=63 mm; P_lenght=216 mm; Pilot_Dia_1=98 mm; Pilot_Dia_2=196 mm; Pilot_Dia_3=65 mm; Pilot_Dia_4=33 mm; Pilot_Dia_5=22 mm  [stored 0.0721785 ft]; Pilot_top_1=839 mm; Pilot_top_ref=126 mm; Profile1_Height=625 mm; Profile1_Length=114 mm; Profile1_Length_2=76 mm; Profile_Dia=30 mm  [stored 0.0984252 ft]; Profile_Dia_2=30 mm  [stored 0.0984252 ft]; Profile_Dia_3=60 mm; Profile_Dia_Ref=15 mm  [stored 0.0492126 ft]; Profile_Dia_Ref_2=60 mm; Profile_height ref=70 mm; T_Height=280 mm; T_Height_2=240 mm; T_Height_Ref_1=40 mm  [stored 0.131234 ft]; T_Height_Ref_2=47 mm; T_ref=822 mm; Top_Profile=669 mm; Top_Profile_Ref=674 mm; W=1210 mm; W_Ref=1168 mm

note: [stored X ft] marks values corroborated as IEEE doubles in the binary element streams (Revit-internal decimal feet)

## geometry (parser evidence)
native form markers: Sweep x4
no freeform markers — native parametric forms only
